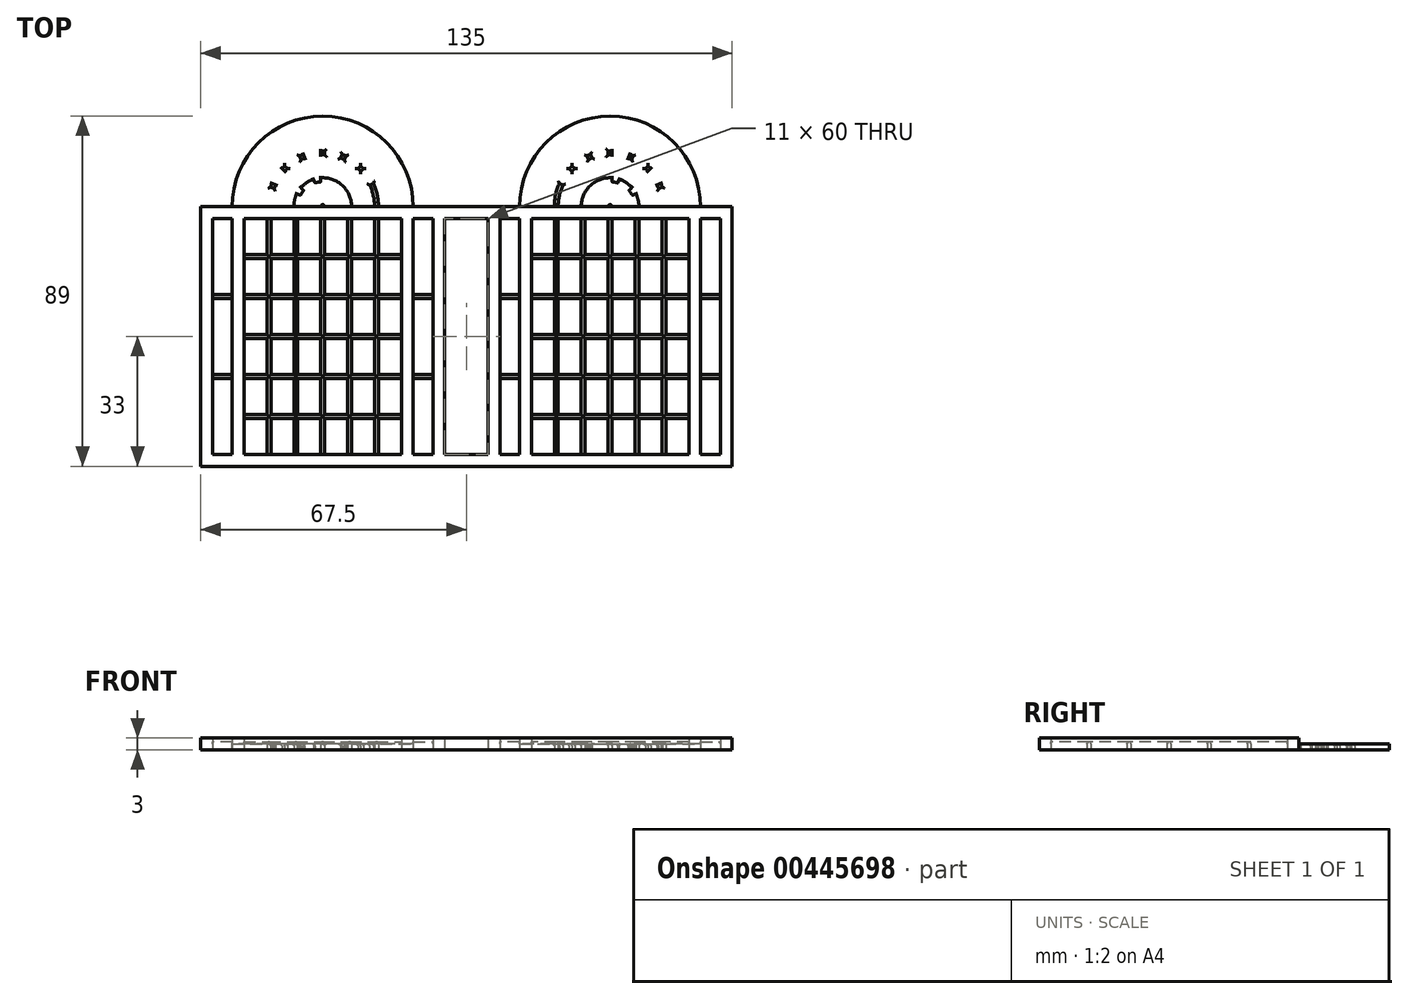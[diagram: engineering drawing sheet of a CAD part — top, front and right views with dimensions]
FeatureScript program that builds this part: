
annotation { "Feature Type Name" : "Feature", "Feature Type Description" : "" }
export const myFeature = defineFeature(function(context is Context, id is Id, definition is map)
    precondition{}
    {
        {
            var Q0;
            Q0=qCreatedBy(makeId("Top.planeOp"),FACE);
            var sketch = newSketch(context, id + "F0", { "sketchPlane" : qUnion([Q0])});
            skLineSegment(sketch, "E0.bottom", {"start": v(0, 0) * mm, "end": v(62, 0) * mm});
            skLineSegment(sketch, "E0.top", {"start": v(0, 60) * mm, "end": v(62, 60) * mm});
            skLineSegment(sketch, "E0.left", {"start": v(0, 0) * mm, "end": v(0, 60) * mm});
            skLineSegment(sketch, "E0.right", {"start": v(62, 0) * mm, "end": v(62, 60) * mm});
            skLineSegment(sketch, "E1", {"start": v(0, 0) * mm, "end": v(8, 0) * mm, "construction": true});
            skLineSegment(sketch, "E2", {"start": v(62, 0) * mm, "end": v(54, 0) * mm, "construction": true});
            skLineSegment(sketch, "E3", {"start": v(62, 0) * mm, "end": v(59, 0) * mm, "construction": true});
            skLineSegment(sketch, "E4", {"start": v(59, 0) * mm, "end": v(59, 60) * mm});
            skLineSegment(sketch, "E5", {"start": v(0, 60) * mm, "end": v(3, 60) * mm, "construction": true});
            skLineSegment(sketch, "E6", {"start": v(3, 60) * mm, "end": v(3, 0) * mm});
            skLineSegment(sketch, "E7", {"start": v(8, 0) * mm, "end": v(8, 60) * mm});
            skLineSegment(sketch, "E8", {"start": v(54, 0) * mm, "end": v(54, 60) * mm});
            skLineSegment(sketch, "E9", {"start": v(8, 0) * mm, "end": v(11, 0) * mm, "construction": true});
            skLineSegment(sketch, "E10", {"start": v(54, 0) * mm, "end": v(51, 0) * mm, "construction": true});
            skLineSegment(sketch, "E11", {"start": v(11, 0) * mm, "end": v(11, 60) * mm});
            skLineSegment(sketch, "E12", {"start": v(51, 0) * mm, "end": v(51, 60) * mm});
            skLineSegment(sketch, "E13.bottom", {"start": v(51, 0) * mm, "end": v(45.17, 0) * mm});
            skLineSegment(sketch, "E13.top", {"start": v(51, 9.17) * mm, "end": v(45.17, 9.17) * mm});
            skLineSegment(sketch, "E13.left", {"start": v(51, 0) * mm, "end": v(51, 9.17) * mm});
            skLineSegment(sketch, "E13.right", {"start": v(45.17, 0) * mm, "end": v(45.17, 9.17) * mm});
            skLineSegment(sketch, "E14.bottom", {"start": v(45.17, 0) * mm, "end": v(44.17, 0) * mm});
            skLineSegment(sketch, "E14.top", {"start": v(45.17, 9.17) * mm, "end": v(44.17, 9.17) * mm, "construction": true});
            skLineSegment(sketch, "E14.right", {"start": v(44.17, 0) * mm, "end": v(44.17, 9.17) * mm});
            skLineSegment(sketch, "E15.top", {"start": v(51, 10.17) * mm, "end": v(45.17, 10.17) * mm});
            skLineSegment(sketch, "E15.left", {"start": v(51, 9.17) * mm, "end": v(51, 10.17) * mm});
            skLineSegment(sketch, "E15.right", {"start": v(45.17, 9.17) * mm, "end": v(45.17, 10.17) * mm, "construction": true});
            skLineSegment(sketch, "E16", {"start": v(44.17, 9.17) * mm, "end": v(44.17, 10.17) * mm, "construction": true});
            skLineSegment(sketch, "E17", {"start": v(44.17, 10.17) * mm, "end": v(45.17, 10.17) * mm, "construction": true});
            skLineSegment(sketch, "E18.0.1.0", {"start": v(44.17, 20.33) * mm, "end": v(45.17, 20.33) * mm, "construction": true});
            skLineSegment(sketch, "E18.0.1.1", {"start": v(51, 20.33) * mm, "end": v(45.17, 20.33) * mm});
            skLineSegment(sketch, "E18.0.1.2", {"start": v(51, 19.33) * mm, "end": v(45.17, 19.33) * mm});
            skLineSegment(sketch, "E18.0.1.3", {"start": v(45.17, 10.17) * mm, "end": v(45.17, 19.33) * mm});
            skLineSegment(sketch, "E18.0.1.4", {"start": v(44.17, 10.17) * mm, "end": v(44.17, 19.33) * mm});
            skLineSegment(sketch, "E18.0.1.5", {"start": v(45.17, 19.33) * mm, "end": v(44.17, 19.33) * mm, "construction": true});
            skLineSegment(sketch, "E18.0.1.6", {"start": v(44.17, 19.33) * mm, "end": v(44.17, 20.33) * mm, "construction": true});
            skLineSegment(sketch, "E18.0.1.7", {"start": v(45.17, 19.33) * mm, "end": v(45.17, 20.33) * mm, "construction": true});
            skLineSegment(sketch, "E18.0.2.0", {"start": v(44.17, 30.5) * mm, "end": v(45.17, 30.5) * mm, "construction": true});
            skLineSegment(sketch, "E18.0.2.1", {"start": v(51, 30.5) * mm, "end": v(45.17, 30.5) * mm});
            skLineSegment(sketch, "E18.0.2.2", {"start": v(51, 29.5) * mm, "end": v(45.17, 29.5) * mm});
            skLineSegment(sketch, "E18.0.2.3", {"start": v(45.17, 20.33) * mm, "end": v(45.17, 29.5) * mm});
            skLineSegment(sketch, "E18.0.2.4", {"start": v(44.17, 20.33) * mm, "end": v(44.17, 29.5) * mm});
            skLineSegment(sketch, "E18.0.2.5", {"start": v(45.17, 29.5) * mm, "end": v(44.17, 29.5) * mm, "construction": true});
            skLineSegment(sketch, "E18.0.2.6", {"start": v(44.17, 29.5) * mm, "end": v(44.17, 30.5) * mm, "construction": true});
            skLineSegment(sketch, "E18.0.2.7", {"start": v(45.17, 29.5) * mm, "end": v(45.17, 30.5) * mm, "construction": true});
            skLineSegment(sketch, "E18.0.3.0", {"start": v(44.17, 40.67) * mm, "end": v(45.17, 40.67) * mm, "construction": true});
            skLineSegment(sketch, "E18.0.3.1", {"start": v(51, 40.67) * mm, "end": v(45.17, 40.67) * mm});
            skLineSegment(sketch, "E18.0.3.2", {"start": v(51, 39.67) * mm, "end": v(45.17, 39.67) * mm});
            skLineSegment(sketch, "E18.0.3.3", {"start": v(45.17, 30.5) * mm, "end": v(45.17, 39.67) * mm});
            skLineSegment(sketch, "E18.0.3.4", {"start": v(44.17, 30.5) * mm, "end": v(44.17, 39.67) * mm});
            skLineSegment(sketch, "E18.0.3.5", {"start": v(45.17, 39.67) * mm, "end": v(44.17, 39.67) * mm, "construction": true});
            skLineSegment(sketch, "E18.0.3.6", {"start": v(44.17, 39.67) * mm, "end": v(44.17, 40.67) * mm, "construction": true});
            skLineSegment(sketch, "E18.0.3.7", {"start": v(45.17, 39.67) * mm, "end": v(45.17, 40.67) * mm, "construction": true});
            skLineSegment(sketch, "E18.0.4.0", {"start": v(44.17, 50.83) * mm, "end": v(45.17, 50.83) * mm, "construction": true});
            skLineSegment(sketch, "E18.0.4.1", {"start": v(51, 50.83) * mm, "end": v(45.17, 50.83) * mm});
            skLineSegment(sketch, "E18.0.4.2", {"start": v(51, 49.83) * mm, "end": v(45.17, 49.83) * mm});
            skLineSegment(sketch, "E18.0.4.3", {"start": v(45.17, 40.67) * mm, "end": v(45.17, 49.83) * mm});
            skLineSegment(sketch, "E18.0.4.4", {"start": v(44.17, 40.67) * mm, "end": v(44.17, 49.83) * mm});
            skLineSegment(sketch, "E18.0.4.5", {"start": v(45.17, 49.83) * mm, "end": v(44.17, 49.83) * mm, "construction": true});
            skLineSegment(sketch, "E18.0.4.6", {"start": v(44.17, 49.83) * mm, "end": v(44.17, 50.83) * mm, "construction": true});
            skLineSegment(sketch, "E18.0.4.7", {"start": v(45.17, 49.83) * mm, "end": v(45.17, 50.83) * mm, "construction": true});
            skLineSegment(sketch, "E18.0.5.2", {"start": v(51, 60) * mm, "end": v(45.17, 60) * mm});
            skLineSegment(sketch, "E18.0.5.3", {"start": v(45.17, 50.83) * mm, "end": v(45.17, 60) * mm});
            skLineSegment(sketch, "E18.0.5.4", {"start": v(44.17, 50.83) * mm, "end": v(44.17, 60) * mm});
            skLineSegment(sketch, "E18.0.5.5", {"start": v(45.17, 60) * mm, "end": v(44.17, 60) * mm, "construction": true});
            skLineSegment(sketch, "E18.1.0.0", {"start": v(37.33, 10.17) * mm, "end": v(38.33, 10.17) * mm, "construction": true});
            skLineSegment(sketch, "E18.1.0.1", {"start": v(44.17, 10.17) * mm, "end": v(38.33, 10.17) * mm});
            skLineSegment(sketch, "E18.1.0.2", {"start": v(44.17, 9.17) * mm, "end": v(38.33, 9.17) * mm});
            skLineSegment(sketch, "E18.1.0.3", {"start": v(38.33, 0) * mm, "end": v(38.33, 9.17) * mm});
            skLineSegment(sketch, "E18.1.0.4", {"start": v(37.33, 0) * mm, "end": v(37.33, 9.17) * mm});
            skLineSegment(sketch, "E18.1.0.5", {"start": v(38.33, 9.17) * mm, "end": v(37.33, 9.17) * mm, "construction": true});
            skLineSegment(sketch, "E18.1.0.6", {"start": v(37.33, 9.17) * mm, "end": v(37.33, 10.17) * mm, "construction": true});
            skLineSegment(sketch, "E18.1.0.7", {"start": v(38.33, 9.17) * mm, "end": v(38.33, 10.17) * mm, "construction": true});
            skLineSegment(sketch, "E18.1.1.0", {"start": v(37.33, 20.33) * mm, "end": v(38.33, 20.33) * mm, "construction": true});
            skLineSegment(sketch, "E18.1.1.1", {"start": v(44.17, 20.33) * mm, "end": v(38.33, 20.33) * mm});
            skLineSegment(sketch, "E18.1.1.2", {"start": v(44.17, 19.33) * mm, "end": v(38.33, 19.33) * mm});
            skLineSegment(sketch, "E18.1.1.3", {"start": v(38.33, 10.17) * mm, "end": v(38.33, 19.33) * mm});
            skLineSegment(sketch, "E18.1.1.4", {"start": v(37.33, 10.17) * mm, "end": v(37.33, 19.33) * mm});
            skLineSegment(sketch, "E18.1.1.5", {"start": v(38.33, 19.33) * mm, "end": v(37.33, 19.33) * mm, "construction": true});
            skLineSegment(sketch, "E18.1.1.6", {"start": v(37.33, 19.33) * mm, "end": v(37.33, 20.33) * mm, "construction": true});
            skLineSegment(sketch, "E18.1.1.7", {"start": v(38.33, 19.33) * mm, "end": v(38.33, 20.33) * mm, "construction": true});
            skLineSegment(sketch, "E18.1.2.0", {"start": v(37.33, 30.5) * mm, "end": v(38.33, 30.5) * mm, "construction": true});
            skLineSegment(sketch, "E18.1.2.1", {"start": v(44.17, 30.5) * mm, "end": v(38.33, 30.5) * mm});
            skLineSegment(sketch, "E18.1.2.2", {"start": v(44.17, 29.5) * mm, "end": v(38.33, 29.5) * mm});
            skLineSegment(sketch, "E18.1.2.3", {"start": v(38.33, 20.33) * mm, "end": v(38.33, 29.5) * mm});
            skLineSegment(sketch, "E18.1.2.4", {"start": v(37.33, 20.33) * mm, "end": v(37.33, 29.5) * mm});
            skLineSegment(sketch, "E18.1.2.5", {"start": v(38.33, 29.5) * mm, "end": v(37.33, 29.5) * mm, "construction": true});
            skLineSegment(sketch, "E18.1.2.6", {"start": v(37.33, 29.5) * mm, "end": v(37.33, 30.5) * mm, "construction": true});
            skLineSegment(sketch, "E18.1.2.7", {"start": v(38.33, 29.5) * mm, "end": v(38.33, 30.5) * mm, "construction": true});
            skLineSegment(sketch, "E18.1.3.0", {"start": v(37.33, 40.67) * mm, "end": v(38.33, 40.67) * mm, "construction": true});
            skLineSegment(sketch, "E18.1.3.1", {"start": v(44.17, 40.67) * mm, "end": v(38.33, 40.67) * mm});
            skLineSegment(sketch, "E18.1.3.2", {"start": v(44.17, 39.67) * mm, "end": v(38.33, 39.67) * mm});
            skLineSegment(sketch, "E18.1.3.3", {"start": v(38.33, 30.5) * mm, "end": v(38.33, 39.67) * mm});
            skLineSegment(sketch, "E18.1.3.4", {"start": v(37.33, 30.5) * mm, "end": v(37.33, 39.67) * mm});
            skLineSegment(sketch, "E18.1.3.5", {"start": v(38.33, 39.67) * mm, "end": v(37.33, 39.67) * mm, "construction": true});
            skLineSegment(sketch, "E18.1.3.6", {"start": v(37.33, 39.67) * mm, "end": v(37.33, 40.67) * mm, "construction": true});
            skLineSegment(sketch, "E18.1.3.7", {"start": v(38.33, 39.67) * mm, "end": v(38.33, 40.67) * mm, "construction": true});
            skLineSegment(sketch, "E18.1.4.0", {"start": v(37.33, 50.83) * mm, "end": v(38.33, 50.83) * mm, "construction": true});
            skLineSegment(sketch, "E18.1.4.1", {"start": v(44.17, 50.83) * mm, "end": v(38.33, 50.83) * mm});
            skLineSegment(sketch, "E18.1.4.2", {"start": v(44.17, 49.83) * mm, "end": v(38.33, 49.83) * mm});
            skLineSegment(sketch, "E18.1.4.3", {"start": v(38.33, 40.67) * mm, "end": v(38.33, 49.83) * mm});
            skLineSegment(sketch, "E18.1.4.4", {"start": v(37.33, 40.67) * mm, "end": v(37.33, 49.83) * mm});
            skLineSegment(sketch, "E18.1.4.5", {"start": v(38.33, 49.83) * mm, "end": v(37.33, 49.83) * mm, "construction": true});
            skLineSegment(sketch, "E18.1.4.6", {"start": v(37.33, 49.83) * mm, "end": v(37.33, 50.83) * mm, "construction": true});
            skLineSegment(sketch, "E18.1.4.7", {"start": v(38.33, 49.83) * mm, "end": v(38.33, 50.83) * mm, "construction": true});
            skLineSegment(sketch, "E18.1.5.2", {"start": v(44.17, 60) * mm, "end": v(38.33, 60) * mm});
            skLineSegment(sketch, "E18.1.5.3", {"start": v(38.33, 50.83) * mm, "end": v(38.33, 60) * mm});
            skLineSegment(sketch, "E18.1.5.4", {"start": v(37.33, 50.83) * mm, "end": v(37.33, 60) * mm});
            skLineSegment(sketch, "E18.1.5.5", {"start": v(38.33, 60) * mm, "end": v(37.33, 60) * mm, "construction": true});
            skLineSegment(sketch, "E18.2.0.0", {"start": v(30.5, 10.17) * mm, "end": v(31.5, 10.17) * mm, "construction": true});
            skLineSegment(sketch, "E18.2.0.1", {"start": v(37.33, 10.17) * mm, "end": v(31.5, 10.17) * mm});
            skLineSegment(sketch, "E18.2.0.2", {"start": v(37.33, 9.17) * mm, "end": v(31.5, 9.17) * mm});
            skLineSegment(sketch, "E18.2.0.3", {"start": v(31.5, 0) * mm, "end": v(31.5, 9.17) * mm});
            skLineSegment(sketch, "E18.2.0.4", {"start": v(30.5, 0) * mm, "end": v(30.5, 9.17) * mm});
            skLineSegment(sketch, "E18.2.0.5", {"start": v(31.5, 9.17) * mm, "end": v(30.5, 9.17) * mm, "construction": true});
            skLineSegment(sketch, "E18.2.0.6", {"start": v(30.5, 9.17) * mm, "end": v(30.5, 10.17) * mm, "construction": true});
            skLineSegment(sketch, "E18.2.0.7", {"start": v(31.5, 9.17) * mm, "end": v(31.5, 10.17) * mm, "construction": true});
            skLineSegment(sketch, "E18.2.1.0", {"start": v(30.5, 20.33) * mm, "end": v(31.5, 20.33) * mm, "construction": true});
            skLineSegment(sketch, "E18.2.1.1", {"start": v(37.33, 20.33) * mm, "end": v(31.5, 20.33) * mm});
            skLineSegment(sketch, "E18.2.1.2", {"start": v(37.33, 19.33) * mm, "end": v(31.5, 19.33) * mm});
            skLineSegment(sketch, "E18.2.1.3", {"start": v(31.5, 10.17) * mm, "end": v(31.5, 19.33) * mm});
            skLineSegment(sketch, "E18.2.1.4", {"start": v(30.5, 10.17) * mm, "end": v(30.5, 19.33) * mm});
            skLineSegment(sketch, "E18.2.1.5", {"start": v(31.5, 19.33) * mm, "end": v(30.5, 19.33) * mm, "construction": true});
            skLineSegment(sketch, "E18.2.1.6", {"start": v(30.5, 19.33) * mm, "end": v(30.5, 20.33) * mm, "construction": true});
            skLineSegment(sketch, "E18.2.1.7", {"start": v(31.5, 19.33) * mm, "end": v(31.5, 20.33) * mm, "construction": true});
            skLineSegment(sketch, "E18.2.2.0", {"start": v(30.5, 30.5) * mm, "end": v(31.5, 30.5) * mm, "construction": true});
            skLineSegment(sketch, "E18.2.2.1", {"start": v(37.33, 30.5) * mm, "end": v(31.5, 30.5) * mm});
            skLineSegment(sketch, "E18.2.2.2", {"start": v(37.33, 29.5) * mm, "end": v(31.5, 29.5) * mm});
            skLineSegment(sketch, "E18.2.2.3", {"start": v(31.5, 20.33) * mm, "end": v(31.5, 29.5) * mm});
            skLineSegment(sketch, "E18.2.2.4", {"start": v(30.5, 20.33) * mm, "end": v(30.5, 29.5) * mm});
            skLineSegment(sketch, "E18.2.2.5", {"start": v(31.5, 29.5) * mm, "end": v(30.5, 29.5) * mm, "construction": true});
            skLineSegment(sketch, "E18.2.2.6", {"start": v(30.5, 29.5) * mm, "end": v(30.5, 30.5) * mm, "construction": true});
            skLineSegment(sketch, "E18.2.2.7", {"start": v(31.5, 29.5) * mm, "end": v(31.5, 30.5) * mm, "construction": true});
            skLineSegment(sketch, "E18.2.3.0", {"start": v(30.5, 40.67) * mm, "end": v(31.5, 40.67) * mm, "construction": true});
            skLineSegment(sketch, "E18.2.3.1", {"start": v(37.33, 40.67) * mm, "end": v(31.5, 40.67) * mm});
            skLineSegment(sketch, "E18.2.3.2", {"start": v(37.33, 39.67) * mm, "end": v(31.5, 39.67) * mm});
            skLineSegment(sketch, "E18.2.3.3", {"start": v(31.5, 30.5) * mm, "end": v(31.5, 39.67) * mm});
            skLineSegment(sketch, "E18.2.3.4", {"start": v(30.5, 30.5) * mm, "end": v(30.5, 39.67) * mm});
            skLineSegment(sketch, "E18.2.3.5", {"start": v(31.5, 39.67) * mm, "end": v(30.5, 39.67) * mm, "construction": true});
            skLineSegment(sketch, "E18.2.3.6", {"start": v(30.5, 39.67) * mm, "end": v(30.5, 40.67) * mm, "construction": true});
            skLineSegment(sketch, "E18.2.3.7", {"start": v(31.5, 39.67) * mm, "end": v(31.5, 40.67) * mm, "construction": true});
            skLineSegment(sketch, "E18.2.4.0", {"start": v(30.5, 50.83) * mm, "end": v(31.5, 50.83) * mm, "construction": true});
            skLineSegment(sketch, "E18.2.4.1", {"start": v(37.33, 50.83) * mm, "end": v(31.5, 50.83) * mm});
            skLineSegment(sketch, "E18.2.4.2", {"start": v(37.33, 49.83) * mm, "end": v(31.5, 49.83) * mm});
            skLineSegment(sketch, "E18.2.4.3", {"start": v(31.5, 40.67) * mm, "end": v(31.5, 49.83) * mm});
            skLineSegment(sketch, "E18.2.4.4", {"start": v(30.5, 40.67) * mm, "end": v(30.5, 49.83) * mm});
            skLineSegment(sketch, "E18.2.4.5", {"start": v(31.5, 49.83) * mm, "end": v(30.5, 49.83) * mm, "construction": true});
            skLineSegment(sketch, "E18.2.4.6", {"start": v(30.5, 49.83) * mm, "end": v(30.5, 50.83) * mm, "construction": true});
            skLineSegment(sketch, "E18.2.4.7", {"start": v(31.5, 49.83) * mm, "end": v(31.5, 50.83) * mm, "construction": true});
            skLineSegment(sketch, "E18.2.5.2", {"start": v(37.33, 60) * mm, "end": v(31.5, 60) * mm});
            skLineSegment(sketch, "E18.2.5.3", {"start": v(31.5, 50.83) * mm, "end": v(31.5, 60) * mm});
            skLineSegment(sketch, "E18.2.5.4", {"start": v(30.5, 50.83) * mm, "end": v(30.5, 60) * mm});
            skLineSegment(sketch, "E18.2.5.5", {"start": v(31.5, 60) * mm, "end": v(30.5, 60) * mm, "construction": true});
            skLineSegment(sketch, "E18.3.0.0", {"start": v(23.67, 10.17) * mm, "end": v(24.67, 10.17) * mm, "construction": true});
            skLineSegment(sketch, "E18.3.0.1", {"start": v(30.5, 10.17) * mm, "end": v(24.67, 10.17) * mm});
            skLineSegment(sketch, "E18.3.0.2", {"start": v(30.5, 9.17) * mm, "end": v(24.67, 9.17) * mm});
            skLineSegment(sketch, "E18.3.0.3", {"start": v(24.67, 0) * mm, "end": v(24.67, 9.17) * mm});
            skLineSegment(sketch, "E18.3.0.4", {"start": v(23.67, 0) * mm, "end": v(23.67, 9.17) * mm});
            skLineSegment(sketch, "E18.3.0.5", {"start": v(24.67, 9.17) * mm, "end": v(23.67, 9.17) * mm, "construction": true});
            skLineSegment(sketch, "E18.3.0.6", {"start": v(23.67, 9.17) * mm, "end": v(23.67, 10.17) * mm, "construction": true});
            skLineSegment(sketch, "E18.3.0.7", {"start": v(24.67, 9.17) * mm, "end": v(24.67, 10.17) * mm, "construction": true});
            skLineSegment(sketch, "E18.3.1.0", {"start": v(23.67, 20.33) * mm, "end": v(24.67, 20.33) * mm, "construction": true});
            skLineSegment(sketch, "E18.3.1.1", {"start": v(30.5, 20.33) * mm, "end": v(24.67, 20.33) * mm});
            skLineSegment(sketch, "E18.3.1.2", {"start": v(30.5, 19.33) * mm, "end": v(24.67, 19.33) * mm});
            skLineSegment(sketch, "E18.3.1.3", {"start": v(24.67, 10.17) * mm, "end": v(24.67, 19.33) * mm});
            skLineSegment(sketch, "E18.3.1.4", {"start": v(23.67, 10.17) * mm, "end": v(23.67, 19.33) * mm});
            skLineSegment(sketch, "E18.3.1.5", {"start": v(24.67, 19.33) * mm, "end": v(23.67, 19.33) * mm, "construction": true});
            skLineSegment(sketch, "E18.3.1.6", {"start": v(23.67, 19.33) * mm, "end": v(23.67, 20.33) * mm, "construction": true});
            skLineSegment(sketch, "E18.3.1.7", {"start": v(24.67, 19.33) * mm, "end": v(24.67, 20.33) * mm, "construction": true});
            skLineSegment(sketch, "E18.3.2.0", {"start": v(23.67, 30.5) * mm, "end": v(24.67, 30.5) * mm, "construction": true});
            skLineSegment(sketch, "E18.3.2.1", {"start": v(30.5, 30.5) * mm, "end": v(24.67, 30.5) * mm});
            skLineSegment(sketch, "E18.3.2.2", {"start": v(30.5, 29.5) * mm, "end": v(24.67, 29.5) * mm});
            skLineSegment(sketch, "E18.3.2.3", {"start": v(24.67, 20.33) * mm, "end": v(24.67, 29.5) * mm});
            skLineSegment(sketch, "E18.3.2.4", {"start": v(23.67, 20.33) * mm, "end": v(23.67, 29.5) * mm});
            skLineSegment(sketch, "E18.3.2.5", {"start": v(24.67, 29.5) * mm, "end": v(23.67, 29.5) * mm, "construction": true});
            skLineSegment(sketch, "E18.3.2.6", {"start": v(23.67, 29.5) * mm, "end": v(23.67, 30.5) * mm, "construction": true});
            skLineSegment(sketch, "E18.3.2.7", {"start": v(24.67, 29.5) * mm, "end": v(24.67, 30.5) * mm, "construction": true});
            skLineSegment(sketch, "E18.3.3.0", {"start": v(23.67, 40.67) * mm, "end": v(24.67, 40.67) * mm, "construction": true});
            skLineSegment(sketch, "E18.3.3.1", {"start": v(30.5, 40.67) * mm, "end": v(24.67, 40.67) * mm});
            skLineSegment(sketch, "E18.3.3.2", {"start": v(30.5, 39.67) * mm, "end": v(24.67, 39.67) * mm});
            skLineSegment(sketch, "E18.3.3.3", {"start": v(24.67, 30.5) * mm, "end": v(24.67, 39.67) * mm});
            skLineSegment(sketch, "E18.3.3.4", {"start": v(23.67, 30.5) * mm, "end": v(23.67, 39.67) * mm});
            skLineSegment(sketch, "E18.3.3.5", {"start": v(24.67, 39.67) * mm, "end": v(23.67, 39.67) * mm, "construction": true});
            skLineSegment(sketch, "E18.3.3.6", {"start": v(23.67, 39.67) * mm, "end": v(23.67, 40.67) * mm, "construction": true});
            skLineSegment(sketch, "E18.3.3.7", {"start": v(24.67, 39.67) * mm, "end": v(24.67, 40.67) * mm, "construction": true});
            skLineSegment(sketch, "E18.3.4.0", {"start": v(23.67, 50.83) * mm, "end": v(24.67, 50.83) * mm, "construction": true});
            skLineSegment(sketch, "E18.3.4.1", {"start": v(30.5, 50.83) * mm, "end": v(24.67, 50.83) * mm});
            skLineSegment(sketch, "E18.3.4.2", {"start": v(30.5, 49.83) * mm, "end": v(24.67, 49.83) * mm});
            skLineSegment(sketch, "E18.3.4.3", {"start": v(24.67, 40.67) * mm, "end": v(24.67, 49.83) * mm});
            skLineSegment(sketch, "E18.3.4.4", {"start": v(23.67, 40.67) * mm, "end": v(23.67, 49.83) * mm});
            skLineSegment(sketch, "E18.3.4.5", {"start": v(24.67, 49.83) * mm, "end": v(23.67, 49.83) * mm, "construction": true});
            skLineSegment(sketch, "E18.3.4.6", {"start": v(23.67, 49.83) * mm, "end": v(23.67, 50.83) * mm, "construction": true});
            skLineSegment(sketch, "E18.3.4.7", {"start": v(24.67, 49.83) * mm, "end": v(24.67, 50.83) * mm, "construction": true});
            skLineSegment(sketch, "E18.3.5.2", {"start": v(30.5, 60) * mm, "end": v(24.67, 60) * mm});
            skLineSegment(sketch, "E18.3.5.3", {"start": v(24.67, 50.83) * mm, "end": v(24.67, 60) * mm});
            skLineSegment(sketch, "E18.3.5.4", {"start": v(23.67, 50.83) * mm, "end": v(23.67, 60) * mm});
            skLineSegment(sketch, "E18.3.5.5", {"start": v(24.67, 60) * mm, "end": v(23.67, 60) * mm, "construction": true});
            skLineSegment(sketch, "E18.4.0.0", {"start": v(16.83, 10.17) * mm, "end": v(17.83, 10.17) * mm, "construction": true});
            skLineSegment(sketch, "E18.4.0.1", {"start": v(23.67, 10.17) * mm, "end": v(17.83, 10.17) * mm});
            skLineSegment(sketch, "E18.4.0.2", {"start": v(23.67, 9.17) * mm, "end": v(17.83, 9.17) * mm});
            skLineSegment(sketch, "E18.4.0.3", {"start": v(17.83, 0) * mm, "end": v(17.83, 9.17) * mm});
            skLineSegment(sketch, "E18.4.0.4", {"start": v(16.83, 0) * mm, "end": v(16.83, 9.17) * mm});
            skLineSegment(sketch, "E18.4.0.5", {"start": v(17.83, 9.17) * mm, "end": v(16.83, 9.17) * mm, "construction": true});
            skLineSegment(sketch, "E18.4.0.6", {"start": v(16.83, 9.17) * mm, "end": v(16.83, 10.17) * mm, "construction": true});
            skLineSegment(sketch, "E18.4.0.7", {"start": v(17.83, 9.17) * mm, "end": v(17.83, 10.17) * mm, "construction": true});
            skLineSegment(sketch, "E18.4.1.0", {"start": v(16.83, 20.33) * mm, "end": v(17.83, 20.33) * mm, "construction": true});
            skLineSegment(sketch, "E18.4.1.1", {"start": v(23.67, 20.33) * mm, "end": v(17.83, 20.33) * mm});
            skLineSegment(sketch, "E18.4.1.2", {"start": v(23.67, 19.33) * mm, "end": v(17.83, 19.33) * mm});
            skLineSegment(sketch, "E18.4.1.3", {"start": v(17.83, 10.17) * mm, "end": v(17.83, 19.33) * mm});
            skLineSegment(sketch, "E18.4.1.4", {"start": v(16.83, 10.17) * mm, "end": v(16.83, 19.33) * mm});
            skLineSegment(sketch, "E18.4.1.5", {"start": v(17.83, 19.33) * mm, "end": v(16.83, 19.33) * mm, "construction": true});
            skLineSegment(sketch, "E18.4.1.6", {"start": v(16.83, 19.33) * mm, "end": v(16.83, 20.33) * mm, "construction": true});
            skLineSegment(sketch, "E18.4.1.7", {"start": v(17.83, 19.33) * mm, "end": v(17.83, 20.33) * mm, "construction": true});
            skLineSegment(sketch, "E18.4.2.0", {"start": v(16.83, 30.5) * mm, "end": v(17.83, 30.5) * mm, "construction": true});
            skLineSegment(sketch, "E18.4.2.1", {"start": v(23.67, 30.5) * mm, "end": v(17.83, 30.5) * mm});
            skLineSegment(sketch, "E18.4.2.2", {"start": v(23.67, 29.5) * mm, "end": v(17.83, 29.5) * mm});
            skLineSegment(sketch, "E18.4.2.3", {"start": v(17.83, 20.33) * mm, "end": v(17.83, 29.5) * mm});
            skLineSegment(sketch, "E18.4.2.4", {"start": v(16.83, 20.33) * mm, "end": v(16.83, 29.5) * mm});
            skLineSegment(sketch, "E18.4.2.5", {"start": v(17.83, 29.5) * mm, "end": v(16.83, 29.5) * mm, "construction": true});
            skLineSegment(sketch, "E18.4.2.6", {"start": v(16.83, 29.5) * mm, "end": v(16.83, 30.5) * mm, "construction": true});
            skLineSegment(sketch, "E18.4.2.7", {"start": v(17.83, 29.5) * mm, "end": v(17.83, 30.5) * mm, "construction": true});
            skLineSegment(sketch, "E18.4.3.0", {"start": v(16.83, 40.67) * mm, "end": v(17.83, 40.67) * mm, "construction": true});
            skLineSegment(sketch, "E18.4.3.1", {"start": v(23.67, 40.67) * mm, "end": v(17.83, 40.67) * mm});
            skLineSegment(sketch, "E18.4.3.2", {"start": v(23.67, 39.67) * mm, "end": v(17.83, 39.67) * mm});
            skLineSegment(sketch, "E18.4.3.3", {"start": v(17.83, 30.5) * mm, "end": v(17.83, 39.67) * mm});
            skLineSegment(sketch, "E18.4.3.4", {"start": v(16.83, 30.5) * mm, "end": v(16.83, 39.67) * mm});
            skLineSegment(sketch, "E18.4.3.5", {"start": v(17.83, 39.67) * mm, "end": v(16.83, 39.67) * mm, "construction": true});
            skLineSegment(sketch, "E18.4.3.6", {"start": v(16.83, 39.67) * mm, "end": v(16.83, 40.67) * mm, "construction": true});
            skLineSegment(sketch, "E18.4.3.7", {"start": v(17.83, 39.67) * mm, "end": v(17.83, 40.67) * mm, "construction": true});
            skLineSegment(sketch, "E18.4.4.0", {"start": v(16.83, 50.83) * mm, "end": v(17.83, 50.83) * mm, "construction": true});
            skLineSegment(sketch, "E18.4.4.1", {"start": v(23.67, 50.83) * mm, "end": v(17.83, 50.83) * mm});
            skLineSegment(sketch, "E18.4.4.2", {"start": v(23.67, 49.83) * mm, "end": v(17.83, 49.83) * mm});
            skLineSegment(sketch, "E18.4.4.3", {"start": v(17.83, 40.67) * mm, "end": v(17.83, 49.83) * mm});
            skLineSegment(sketch, "E18.4.4.4", {"start": v(16.83, 40.67) * mm, "end": v(16.83, 49.83) * mm});
            skLineSegment(sketch, "E18.4.4.5", {"start": v(17.83, 49.83) * mm, "end": v(16.83, 49.83) * mm, "construction": true});
            skLineSegment(sketch, "E18.4.4.6", {"start": v(16.83, 49.83) * mm, "end": v(16.83, 50.83) * mm, "construction": true});
            skLineSegment(sketch, "E18.4.4.7", {"start": v(17.83, 49.83) * mm, "end": v(17.83, 50.83) * mm, "construction": true});
            skLineSegment(sketch, "E18.4.5.2", {"start": v(23.67, 60) * mm, "end": v(17.83, 60) * mm});
            skLineSegment(sketch, "E18.4.5.3", {"start": v(17.83, 50.83) * mm, "end": v(17.83, 60) * mm});
            skLineSegment(sketch, "E18.4.5.4", {"start": v(16.83, 50.83) * mm, "end": v(16.83, 60) * mm});
            skLineSegment(sketch, "E18.4.5.5", {"start": v(17.83, 60) * mm, "end": v(16.83, 60) * mm, "construction": true});
            skLineSegment(sketch, "E18.5.0.1", {"start": v(16.83, 10.17) * mm, "end": v(11, 10.17) * mm});
            skLineSegment(sketch, "E18.5.0.2", {"start": v(16.83, 9.17) * mm, "end": v(11, 9.17) * mm});
            skLineSegment(sketch, "E18.5.0.3", {"start": v(11, 0) * mm, "end": v(11, 9.17) * mm});
            skLineSegment(sketch, "E18.5.0.7", {"start": v(11, 9.17) * mm, "end": v(11, 10.17) * mm, "construction": true});
            skLineSegment(sketch, "E18.5.1.1", {"start": v(16.83, 20.33) * mm, "end": v(11, 20.33) * mm});
            skLineSegment(sketch, "E18.5.1.2", {"start": v(16.83, 19.33) * mm, "end": v(11, 19.33) * mm});
            skLineSegment(sketch, "E18.5.1.3", {"start": v(11, 10.17) * mm, "end": v(11, 19.33) * mm});
            skLineSegment(sketch, "E18.5.1.7", {"start": v(11, 19.33) * mm, "end": v(11, 20.33) * mm, "construction": true});
            skLineSegment(sketch, "E18.5.2.1", {"start": v(16.83, 30.5) * mm, "end": v(11, 30.5) * mm});
            skLineSegment(sketch, "E18.5.2.2", {"start": v(16.83, 29.5) * mm, "end": v(11, 29.5) * mm});
            skLineSegment(sketch, "E18.5.2.3", {"start": v(11, 20.33) * mm, "end": v(11, 29.5) * mm});
            skLineSegment(sketch, "E18.5.2.7", {"start": v(11, 29.5) * mm, "end": v(11, 30.5) * mm, "construction": true});
            skLineSegment(sketch, "E18.5.3.1", {"start": v(16.83, 40.67) * mm, "end": v(11, 40.67) * mm});
            skLineSegment(sketch, "E18.5.3.2", {"start": v(16.83, 39.67) * mm, "end": v(11, 39.67) * mm});
            skLineSegment(sketch, "E18.5.3.3", {"start": v(11, 30.5) * mm, "end": v(11, 39.67) * mm});
            skLineSegment(sketch, "E18.5.3.7", {"start": v(11, 39.67) * mm, "end": v(11, 40.67) * mm, "construction": true});
            skLineSegment(sketch, "E18.5.4.1", {"start": v(16.83, 50.83) * mm, "end": v(11, 50.83) * mm});
            skLineSegment(sketch, "E18.5.4.2", {"start": v(16.83, 49.83) * mm, "end": v(11, 49.83) * mm});
            skLineSegment(sketch, "E18.5.4.3", {"start": v(11, 40.67) * mm, "end": v(11, 49.83) * mm});
            skLineSegment(sketch, "E18.5.4.7", {"start": v(11, 49.83) * mm, "end": v(11, 50.83) * mm, "construction": true});
            skLineSegment(sketch, "E18.5.5.2", {"start": v(16.83, 60) * mm, "end": v(11, 60) * mm});
            skLineSegment(sketch, "E18.5.5.3", {"start": v(11, 50.83) * mm, "end": v(11, 60) * mm});
            skLineSegment(sketch, "E18.direction1", {"start": v(44.17, 0) * mm, "end": v(37.33, 0) * mm, "construction": true});
            skLineSegment(sketch, "E18.direction2", {"start": v(44.17, 0) * mm, "end": v(44.17, 10.17) * mm, "construction": true});
            skLineSegment(sketch, "E19.top", {"start": v(0, -3) * mm, "end": v(62, -3) * mm});
            skLineSegment(sketch, "E19.left", {"start": v(0, 0) * mm, "end": v(0, -3) * mm});
            skLineSegment(sketch, "E19.right", {"start": v(62, 0) * mm, "end": v(62, -3) * mm});
            skLineSegment(sketch, "E20.top", {"start": v(0, 63) * mm, "end": v(62, 63) * mm});
            skLineSegment(sketch, "E20.left", {"start": v(0, 60) * mm, "end": v(0, 63) * mm});
            skLineSegment(sketch, "E20.right", {"start": v(62, 60) * mm, "end": v(62, 63) * mm});
            skLineSegment(sketch, "E21", {"start": v(31, 63) * mm, "end": v(31, 86) * mm, "construction": true});
            skArc(sketch, "E22", {"start": v(11, 63) * mm, "mid": v(31, 83) * mm, "end": v(51, 63) * mm});
            skArc(sketch, "E23", {"start": v(8, 63) * mm, "mid": v(31, 86) * mm, "end": v(54, 63) * mm});
            skArc(sketch, "E24", {"start": v(16.83, 63) * mm, "mid": v(31, 77.17) * mm, "end": v(45.17, 63) * mm});
            skArc(sketch, "E25", {"start": v(17.83, 63) * mm, "mid": v(31, 76.17) * mm, "end": v(44.17, 63) * mm});
            skArc(sketch, "E26", {"start": v(23.67, 63) * mm, "mid": v(31, 70.33) * mm, "end": v(38.33, 63) * mm});
            skArc(sketch, "E27", {"start": v(24.67, 63) * mm, "mid": v(31, 69.33) * mm, "end": v(37.33, 63) * mm});
            skArc(sketch, "E28", {"start": v(30.5, 63) * mm, "mid": v(31, 63.5) * mm, "end": v(31.5, 63) * mm});
            skLineSegment(sketch, "E29", {"start": v(31, 63) * mm, "end": v(8, 63) * mm});
            skLineSegment(sketch, "E30.1.0", {"start": v(31, 63) * mm, "end": v(9.75, 71.8) * mm, "construction": true});
            skLineSegment(sketch, "E30.2.0", {"start": v(31, 63) * mm, "end": v(14.74, 79.26) * mm, "construction": true});
            skLineSegment(sketch, "E30.3.0", {"start": v(31, 63) * mm, "end": v(22.2, 84.25) * mm, "construction": true});
            skLineSegment(sketch, "E30.5.0", {"start": v(31, 63) * mm, "end": v(39.8, 84.25) * mm, "construction": true});
            skLineSegment(sketch, "E30.6.0", {"start": v(31, 63) * mm, "end": v(47.26, 79.26) * mm, "construction": true});
            skLineSegment(sketch, "E30.7.0", {"start": v(31, 63) * mm, "end": v(52.25, 71.8) * mm, "construction": true});
            skLineSegment(sketch, "E30.8.0", {"start": v(31, 63) * mm, "end": v(54, 63) * mm});
            skLineSegment(sketch, "E30.anchor1", {"start": v(31, 63) * mm, "end": v(8, 63) * mm, "construction": true});
            skLineSegment(sketch, "E30.anchor2", {"start": v(31, 63) * mm, "end": v(54, 63) * mm, "construction": true});
            skLineSegment(sketch, "E31.0", {"start": v(30.08, 63.92) * mm, "end": v(12.72, 71.11) * mm});
            skLineSegment(sketch, "E32.MirrorCS", {"start": v(29.7, 63) * mm, "end": v(12.34, 70.19) * mm});
            skLineSegment(sketch, "E33.0", {"start": v(30.5, 64.2) * mm, "end": v(17.22, 77.5) * mm});
            skLineSegment(sketch, "E34.MirrorCS", {"start": v(28.87, 64.42) * mm, "end": v(16.5, 76.78) * mm});
            skLineSegment(sketch, "E35.0", {"start": v(31, 64.3) * mm, "end": v(23.81, 81.66) * mm});
            skLineSegment(sketch, "E36.MirrorCS", {"start": v(30.08, 63.92) * mm, "end": v(22.89, 81.28) * mm});
            skLineSegment(sketch, "E37.0", {"start": v(31.5, 65.51) * mm, "end": v(31.5, 83) * mm});
            skLineSegment(sketch, "E38.0", {"start": v(30.5, 65.51) * mm, "end": v(30.5, 83) * mm});
            skLineSegment(sketch, "E39.0", {"start": v(32.42, 65.13) * mm, "end": v(39.11, 81.28) * mm});
            skLineSegment(sketch, "E40.0", {"start": v(31, 64.3) * mm, "end": v(38.19, 81.66) * mm});
            skLineSegment(sketch, "E41.0", {"start": v(32.3, 63) * mm, "end": v(49.66, 70.19) * mm});
            skLineSegment(sketch, "E42.0", {"start": v(33.13, 64.42) * mm, "end": v(49.28, 71.11) * mm});
            skLineSegment(sketch, "E43.0", {"start": v(33.13, 64.42) * mm, "end": v(45.5, 76.78) * mm});
            skLineSegment(sketch, "E44.0", {"start": v(32.42, 65.13) * mm, "end": v(44.78, 77.5) * mm});
            skSolve(sketch);
        }
        {
            var Q0;
            {var subQ13=sQuery(id+"F0.wireOp",EDGE,"E23");Q0=makeQuery(id+"F0.imprint","IMPRINT",FACE,{"disambiguationData":[TD([[makeQuery(id+"F0.imprint","IMPRINT",EDGE,{"derivedFrom":subQ13}),-1.0]])]});}
            var Q1;
            {var subQ1=sQuery(id+"F0.wireOp",EDGE,"E20.left");Q1=makeQuery(id+"F0.imprint","IMPRINT",FACE,{"disambiguationData":[TD([[makeQuery(id+"F0.imprint","IMPRINT",EDGE,{"derivedFrom":subQ1}),-1.0]])]});}
            var Q2;
            {var subQ0=sQuery(id+"F0.wireOp",EDGE,"E0.right");Q2=makeQuery(id+"F0.imprint","IMPRINT",FACE,{"disambiguationData":[TD([[makeQuery(id+"F0.imprint","IMPRINT",EDGE,{"derivedFrom":subQ0}),1.0]])]});}
            var Q3;
            {var subQ7=sQuery(id+"F0.wireOp",EDGE,"E7");Q3=makeQuery(id+"F0.imprint","IMPRINT",FACE,{"disambiguationData":[TD([[makeQuery(id+"F0.imprint","IMPRINT",EDGE,{"derivedFrom":subQ7}),-1.0]])]});}
            var Q4;
            {var subQ0=sQuery(id+"F0.wireOp",EDGE,"E0.left");Q4=makeQuery(id+"F0.imprint","IMPRINT",FACE,{"disambiguationData":[TD([[makeQuery(id+"F0.imprint","IMPRINT",EDGE,{"derivedFrom":subQ0}),-1.0]])]});}
            var Q5;
            {var subQ9=sQuery(id+"F0.wireOp",EDGE,"E8");Q5=makeQuery(id+"F0.imprint","IMPRINT",FACE,{"disambiguationData":[TD([[makeQuery(id+"F0.imprint","IMPRINT",EDGE,{"derivedFrom":subQ9}),1.0]])]});}
            var Q6;
            Q6=makeQuery(id+"F0.imprint","IMPRINT",FACE,{"disambiguationData":[TD([[makeQuery(id+"F0.imprint","IMPRINT",EDGE,{"derivedFrom":sQuery(id+"F0.wireOp",EDGE,"E19.top")}),1.0]])]});
            extrude(context, id + "F1", {"entities" : qUnion([Q0, Q1, Q2, Q3, Q4, Q5, Q6]), "depth" : 3 * mm});
        }
        {
            var Q0;
            {var subQ0=sQuery(id+"F0.wireOp",EDGE,"E29");var subQ1=sQuery(id+"F0.wireOp",EDGE,"E24");var subQ2=makeQuery(id+"F0.imprint","INTERSECT",VERTEX,{"derivedFrom":[subQ1,subQ0]});Q0=makeQuery(id+"F0.imprint","IMPRINT",FACE,{"disambiguationData":[TD([[makeQuery(id+"F0.imprint","IMPRINT",EDGE,{"disambiguationData":[TD([[subQ2,-1.0]])],"derivedFrom":subQ1}),-1.0]])]});}
            var Q1;
            {var subQ0=sQuery(id+"F0.wireOp",EDGE,"E31.0");var subQ1=sQuery(id+"F0.wireOp",EDGE,"E24");var subQ2=makeQuery(id+"F0.imprint","INTERSECT",VERTEX,{"derivedFrom":[subQ1,subQ0]});Q1=makeQuery(id+"F0.imprint","IMPRINT",FACE,{"disambiguationData":[TD([[makeQuery(id+"F0.imprint","IMPRINT",EDGE,{"disambiguationData":[TD([[subQ2,-1.0]])],"derivedFrom":subQ1}),-1.0]])]});}
            var Q2;
            {var subQ0=sQuery(id+"F0.wireOp",EDGE,"E35.0");var subQ1=sQuery(id+"F0.wireOp",EDGE,"E24");var subQ2=makeQuery(id+"F0.imprint","INTERSECT",VERTEX,{"derivedFrom":[subQ1,subQ0]});Q2=makeQuery(id+"F0.imprint","IMPRINT",FACE,{"disambiguationData":[TD([[makeQuery(id+"F0.imprint","IMPRINT",EDGE,{"disambiguationData":[TD([[subQ2,-1.0]])],"derivedFrom":subQ1}),-1.0]])]});}
            var Q3;
            {var subQ0=sQuery(id+"F0.wireOp",EDGE,"E37.0");var subQ1=sQuery(id+"F0.wireOp",EDGE,"E24");var subQ2=makeQuery(id+"F0.imprint","INTERSECT",VERTEX,{"derivedFrom":[subQ1,subQ0]});Q3=makeQuery(id+"F0.imprint","IMPRINT",FACE,{"disambiguationData":[TD([[makeQuery(id+"F0.imprint","IMPRINT",EDGE,{"disambiguationData":[TD([[subQ2,-1.0]])],"derivedFrom":subQ1}),-1.0]])]});}
            var Q4;
            {var subQ0=sQuery(id+"F0.wireOp",EDGE,"E39.0");var subQ1=sQuery(id+"F0.wireOp",EDGE,"E24");var subQ2=makeQuery(id+"F0.imprint","INTERSECT",VERTEX,{"derivedFrom":[subQ1,subQ0]});Q4=makeQuery(id+"F0.imprint","IMPRINT",FACE,{"disambiguationData":[TD([[makeQuery(id+"F0.imprint","IMPRINT",EDGE,{"disambiguationData":[TD([[subQ2,-1.0]])],"derivedFrom":subQ1}),-1.0]])]});}
            var Q5;
            {var subQ0=sQuery(id+"F0.wireOp",EDGE,"E43.0");var subQ1=sQuery(id+"F0.wireOp",EDGE,"E24");var subQ2=makeQuery(id+"F0.imprint","INTERSECT",VERTEX,{"derivedFrom":[subQ1,subQ0]});Q5=makeQuery(id+"F0.imprint","IMPRINT",FACE,{"disambiguationData":[TD([[makeQuery(id+"F0.imprint","IMPRINT",EDGE,{"disambiguationData":[TD([[subQ2,-1.0]])],"derivedFrom":subQ1}),-1.0]])]});}
            var Q6;
            {var subQ0=sQuery(id+"F0.wireOp",EDGE,"E30.8.0");var subQ1=sQuery(id+"F0.wireOp",EDGE,"E24");var subQ2=makeQuery(id+"F0.imprint","INTERSECT",VERTEX,{"derivedFrom":[subQ1,subQ0]});Q6=makeQuery(id+"F0.imprint","IMPRINT",FACE,{"disambiguationData":[TD([[makeQuery(id+"F0.imprint","IMPRINT",EDGE,{"disambiguationData":[TD([[subQ2,1.0]])],"derivedFrom":subQ1}),-1.0]])]});}
            var Q7;
            {var subQ0=sQuery(id+"F0.wireOp",EDGE,"E33.0");var subQ1=sQuery(id+"F0.wireOp",EDGE,"E22");var subQ2=makeQuery(id+"F0.imprint","INTERSECT",VERTEX,{"derivedFrom":[subQ1,subQ0]});Q7=makeQuery(id+"F0.imprint","IMPRINT",FACE,{"disambiguationData":[TD([[makeQuery(id+"F0.imprint","IMPRINT",EDGE,{"disambiguationData":[TD([[subQ2,1.0]])],"derivedFrom":subQ1}),-1.0]])]});}
            var Q8;
            {var subQ0=sQuery(id+"F0.wireOp",EDGE,"E31.0");var subQ1=sQuery(id+"F0.wireOp",EDGE,"E22");var subQ2=makeQuery(id+"F0.imprint","INTERSECT",VERTEX,{"derivedFrom":[subQ1,subQ0]});Q8=makeQuery(id+"F0.imprint","IMPRINT",FACE,{"disambiguationData":[TD([[makeQuery(id+"F0.imprint","IMPRINT",EDGE,{"disambiguationData":[TD([[subQ2,1.0]])],"derivedFrom":subQ1}),-1.0]])]});}
            var Q9;
            {var subQ0=sQuery(id+"F0.wireOp",EDGE,"E35.0");var subQ1=sQuery(id+"F0.wireOp",EDGE,"E22");var subQ2=makeQuery(id+"F0.imprint","INTERSECT",VERTEX,{"derivedFrom":[subQ1,subQ0]});Q9=makeQuery(id+"F0.imprint","IMPRINT",FACE,{"disambiguationData":[TD([[makeQuery(id+"F0.imprint","IMPRINT",EDGE,{"disambiguationData":[TD([[subQ2,1.0]])],"derivedFrom":subQ1}),-1.0]])]});}
            var Q10;
            {var subQ0=sQuery(id+"F0.wireOp",EDGE,"E37.0");var subQ1=sQuery(id+"F0.wireOp",EDGE,"E22");var subQ2=makeQuery(id+"F0.imprint","INTERSECT",VERTEX,{"derivedFrom":[subQ1,subQ0]});Q10=makeQuery(id+"F0.imprint","IMPRINT",FACE,{"disambiguationData":[TD([[makeQuery(id+"F0.imprint","IMPRINT",EDGE,{"disambiguationData":[TD([[subQ2,1.0]])],"derivedFrom":subQ1}),-1.0]])]});}
            var Q11;
            {var subQ0=sQuery(id+"F0.wireOp",EDGE,"E39.0");var subQ1=sQuery(id+"F0.wireOp",EDGE,"E22");var subQ2=makeQuery(id+"F0.imprint","INTERSECT",VERTEX,{"derivedFrom":[subQ1,subQ0]});Q11=makeQuery(id+"F0.imprint","IMPRINT",FACE,{"disambiguationData":[TD([[makeQuery(id+"F0.imprint","IMPRINT",EDGE,{"disambiguationData":[TD([[subQ2,1.0]])],"derivedFrom":subQ1}),-1.0]])]});}
            var Q12;
            {var subQ0=sQuery(id+"F0.wireOp",EDGE,"E43.0");var subQ1=sQuery(id+"F0.wireOp",EDGE,"E22");var subQ2=makeQuery(id+"F0.imprint","INTERSECT",VERTEX,{"derivedFrom":[subQ1,subQ0]});Q12=makeQuery(id+"F0.imprint","IMPRINT",FACE,{"disambiguationData":[TD([[makeQuery(id+"F0.imprint","IMPRINT",EDGE,{"disambiguationData":[TD([[subQ2,1.0]])],"derivedFrom":subQ1}),-1.0]])]});}
            var Q13;
            {var subQ0=sQuery(id+"F0.wireOp",EDGE,"E41.0");var subQ1=sQuery(id+"F0.wireOp",EDGE,"E22");var subQ2=makeQuery(id+"F0.imprint","INTERSECT",VERTEX,{"derivedFrom":[subQ1,subQ0]});Q13=makeQuery(id+"F0.imprint","IMPRINT",FACE,{"disambiguationData":[TD([[makeQuery(id+"F0.imprint","IMPRINT",EDGE,{"disambiguationData":[TD([[subQ2,1.0]])],"derivedFrom":subQ1}),-1.0]])]});}
            var Q14;
            {var subQ0=sQuery(id+"F0.wireOp",EDGE,"E42.0");var subQ1=sQuery(id+"F0.wireOp",EDGE,"E24");var subQ2=makeQuery(id+"F0.imprint","INTERSECT",VERTEX,{"derivedFrom":[subQ1,subQ0]});Q14=makeQuery(id+"F0.imprint","IMPRINT",FACE,{"disambiguationData":[TD([[makeQuery(id+"F0.imprint","IMPRINT",EDGE,{"disambiguationData":[TD([[subQ2,-1.0]])],"derivedFrom":subQ1}),-1.0]])]});}
            var Q15;
            {var subQ0=sQuery(id+"F0.wireOp",EDGE,"E44.0");var subQ1=sQuery(id+"F0.wireOp",EDGE,"E24");var subQ2=makeQuery(id+"F0.imprint","INTERSECT",VERTEX,{"derivedFrom":[subQ1,subQ0]});Q15=makeQuery(id+"F0.imprint","IMPRINT",FACE,{"disambiguationData":[TD([[makeQuery(id+"F0.imprint","IMPRINT",EDGE,{"disambiguationData":[TD([[subQ2,-1.0]])],"derivedFrom":subQ1}),-1.0]])]});}
            var Q16;
            {var subQ0=sQuery(id+"F0.wireOp",EDGE,"E40.0");var subQ1=sQuery(id+"F0.wireOp",EDGE,"E24");var subQ2=makeQuery(id+"F0.imprint","INTERSECT",VERTEX,{"derivedFrom":[subQ1,subQ0]});Q16=makeQuery(id+"F0.imprint","IMPRINT",FACE,{"disambiguationData":[TD([[makeQuery(id+"F0.imprint","IMPRINT",EDGE,{"disambiguationData":[TD([[subQ2,-1.0]])],"derivedFrom":subQ1}),-1.0]])]});}
            var Q17;
            {var subQ0=sQuery(id+"F0.wireOp",EDGE,"E38.0");var subQ1=sQuery(id+"F0.wireOp",EDGE,"E24");var subQ2=makeQuery(id+"F0.imprint","INTERSECT",VERTEX,{"derivedFrom":[subQ1,subQ0]});Q17=makeQuery(id+"F0.imprint","IMPRINT",FACE,{"disambiguationData":[TD([[makeQuery(id+"F0.imprint","IMPRINT",EDGE,{"disambiguationData":[TD([[subQ2,-1.0]])],"derivedFrom":subQ1}),-1.0]])]});}
            var Q18;
            {var subQ0=sQuery(id+"F0.wireOp",EDGE,"E36.MirrorCS");var subQ1=sQuery(id+"F0.wireOp",EDGE,"E24");var subQ2=makeQuery(id+"F0.imprint","INTERSECT",VERTEX,{"derivedFrom":[subQ1,subQ0]});Q18=makeQuery(id+"F0.imprint","IMPRINT",FACE,{"disambiguationData":[TD([[makeQuery(id+"F0.imprint","IMPRINT",EDGE,{"disambiguationData":[TD([[subQ2,-1.0]])],"derivedFrom":subQ1}),-1.0]])]});}
            var Q19;
            {var subQ0=sQuery(id+"F0.wireOp",EDGE,"E34.MirrorCS");var subQ1=sQuery(id+"F0.wireOp",EDGE,"E24");var subQ2=makeQuery(id+"F0.imprint","INTERSECT",VERTEX,{"derivedFrom":[subQ1,subQ0]});Q19=makeQuery(id+"F0.imprint","IMPRINT",FACE,{"disambiguationData":[TD([[makeQuery(id+"F0.imprint","IMPRINT",EDGE,{"disambiguationData":[TD([[subQ2,-1.0]])],"derivedFrom":subQ1}),-1.0]])]});}
            var Q20;
            {var subQ0=sQuery(id+"F0.wireOp",EDGE,"E32.MirrorCS");var subQ1=sQuery(id+"F0.wireOp",EDGE,"E24");var subQ2=makeQuery(id+"F0.imprint","INTERSECT",VERTEX,{"derivedFrom":[subQ1,subQ0]});Q20=makeQuery(id+"F0.imprint","IMPRINT",FACE,{"disambiguationData":[TD([[makeQuery(id+"F0.imprint","IMPRINT",EDGE,{"disambiguationData":[TD([[subQ2,-1.0]])],"derivedFrom":subQ1}),-1.0]])]});}
            var Q21;
            {var subQ0=sQuery(id+"F0.wireOp",EDGE,"E32.MirrorCS");var subQ1=sQuery(id+"F0.wireOp",EDGE,"E25");var subQ2=makeQuery(id+"F0.imprint","INTERSECT",VERTEX,{"derivedFrom":[subQ1,subQ0]});Q21=makeQuery(id+"F0.imprint","IMPRINT",FACE,{"disambiguationData":[TD([[makeQuery(id+"F0.imprint","IMPRINT",EDGE,{"disambiguationData":[TD([[subQ2,-1.0]])],"derivedFrom":subQ1}),-1.0]])]});}
            var Q22;
            {var subQ0=sQuery(id+"F0.wireOp",EDGE,"E34.MirrorCS");var subQ1=sQuery(id+"F0.wireOp",EDGE,"E25");var subQ2=makeQuery(id+"F0.imprint","INTERSECT",VERTEX,{"derivedFrom":[subQ1,subQ0]});Q22=makeQuery(id+"F0.imprint","IMPRINT",FACE,{"disambiguationData":[TD([[makeQuery(id+"F0.imprint","IMPRINT",EDGE,{"disambiguationData":[TD([[subQ2,-1.0]])],"derivedFrom":subQ1}),-1.0]])]});}
            var Q23;
            {var subQ0=sQuery(id+"F0.wireOp",EDGE,"E36.MirrorCS");var subQ1=sQuery(id+"F0.wireOp",EDGE,"E25");var subQ2=makeQuery(id+"F0.imprint","INTERSECT",VERTEX,{"derivedFrom":[subQ1,subQ0]});Q23=makeQuery(id+"F0.imprint","IMPRINT",FACE,{"disambiguationData":[TD([[makeQuery(id+"F0.imprint","IMPRINT",EDGE,{"disambiguationData":[TD([[subQ2,-1.0]])],"derivedFrom":subQ1}),-1.0]])]});}
            var Q24;
            {var subQ0=sQuery(id+"F0.wireOp",EDGE,"E38.0");var subQ1=sQuery(id+"F0.wireOp",EDGE,"E25");var subQ2=makeQuery(id+"F0.imprint","INTERSECT",VERTEX,{"derivedFrom":[subQ1,subQ0]});Q24=makeQuery(id+"F0.imprint","IMPRINT",FACE,{"disambiguationData":[TD([[makeQuery(id+"F0.imprint","IMPRINT",EDGE,{"disambiguationData":[TD([[subQ2,-1.0]])],"derivedFrom":subQ1}),-1.0]])]});}
            var Q25;
            {var subQ0=sQuery(id+"F0.wireOp",EDGE,"E40.0");var subQ1=sQuery(id+"F0.wireOp",EDGE,"E25");var subQ2=makeQuery(id+"F0.imprint","INTERSECT",VERTEX,{"derivedFrom":[subQ1,subQ0]});Q25=makeQuery(id+"F0.imprint","IMPRINT",FACE,{"disambiguationData":[TD([[makeQuery(id+"F0.imprint","IMPRINT",EDGE,{"disambiguationData":[TD([[subQ2,-1.0]])],"derivedFrom":subQ1}),-1.0]])]});}
            var Q26;
            {var subQ0=sQuery(id+"F0.wireOp",EDGE,"E44.0");var subQ1=sQuery(id+"F0.wireOp",EDGE,"E25");var subQ2=makeQuery(id+"F0.imprint","INTERSECT",VERTEX,{"derivedFrom":[subQ1,subQ0]});Q26=makeQuery(id+"F0.imprint","IMPRINT",FACE,{"disambiguationData":[TD([[makeQuery(id+"F0.imprint","IMPRINT",EDGE,{"disambiguationData":[TD([[subQ2,-1.0]])],"derivedFrom":subQ1}),-1.0]])]});}
            var Q27;
            {var subQ0=sQuery(id+"F0.wireOp",EDGE,"E42.0");var subQ1=sQuery(id+"F0.wireOp",EDGE,"E25");var subQ2=makeQuery(id+"F0.imprint","INTERSECT",VERTEX,{"derivedFrom":[subQ1,subQ0]});Q27=makeQuery(id+"F0.imprint","IMPRINT",FACE,{"disambiguationData":[TD([[makeQuery(id+"F0.imprint","IMPRINT",EDGE,{"disambiguationData":[TD([[subQ2,-1.0]])],"derivedFrom":subQ1}),-1.0]])]});}
            var Q28;
            {var subQ0=sQuery(id+"F0.wireOp",EDGE,"E30.8.0");var subQ1=sQuery(id+"F0.wireOp",EDGE,"E26");var subQ2=makeQuery(id+"F0.imprint","INTERSECT",VERTEX,{"derivedFrom":[subQ1,subQ0]});Q28=makeQuery(id+"F0.imprint","IMPRINT",FACE,{"disambiguationData":[TD([[makeQuery(id+"F0.imprint","IMPRINT",EDGE,{"disambiguationData":[TD([[subQ2,1.0]])],"derivedFrom":subQ1}),-1.0]])]});}
            var Q29;
            {var subQ0=sQuery(id+"F0.wireOp",EDGE,"E42.0");var subQ1=sQuery(id+"F0.wireOp",EDGE,"E26");var subQ2=makeQuery(id+"F0.imprint","INTERSECT",VERTEX,{"derivedFrom":[subQ1,subQ0]});Q29=makeQuery(id+"F0.imprint","IMPRINT",FACE,{"disambiguationData":[TD([[makeQuery(id+"F0.imprint","IMPRINT",EDGE,{"disambiguationData":[TD([[subQ2,-1.0]])],"derivedFrom":subQ1}),-1.0]])]});}
            var Q30;
            {var subQ0=sQuery(id+"F0.wireOp",EDGE,"E43.0");var subQ1=sQuery(id+"F0.wireOp",EDGE,"E26");var subQ2=makeQuery(id+"F0.imprint","INTERSECT",VERTEX,{"derivedFrom":[subQ1,subQ0]});Q30=makeQuery(id+"F0.imprint","IMPRINT",FACE,{"disambiguationData":[TD([[makeQuery(id+"F0.imprint","IMPRINT",EDGE,{"disambiguationData":[TD([[subQ2,-1.0]])],"derivedFrom":subQ1}),-1.0]])]});}
            var Q31;
            {var subQ0=sQuery(id+"F0.wireOp",EDGE,"E44.0");var subQ1=sQuery(id+"F0.wireOp",EDGE,"E26");var subQ2=makeQuery(id+"F0.imprint","INTERSECT",VERTEX,{"derivedFrom":[subQ1,subQ0]});Q31=makeQuery(id+"F0.imprint","IMPRINT",FACE,{"disambiguationData":[TD([[makeQuery(id+"F0.imprint","IMPRINT",EDGE,{"disambiguationData":[TD([[subQ2,-1.0]])],"derivedFrom":subQ1}),-1.0]])]});}
            var Q32;
            {var subQ0=sQuery(id+"F0.wireOp",EDGE,"E39.0");var subQ1=sQuery(id+"F0.wireOp",EDGE,"E26");var subQ2=makeQuery(id+"F0.imprint","INTERSECT",VERTEX,{"derivedFrom":[subQ1,subQ0]});Q32=makeQuery(id+"F0.imprint","IMPRINT",FACE,{"disambiguationData":[TD([[makeQuery(id+"F0.imprint","IMPRINT",EDGE,{"disambiguationData":[TD([[subQ2,-1.0]])],"derivedFrom":subQ1}),-1.0]])]});}
            var Q33;
            {var subQ0=sQuery(id+"F0.wireOp",EDGE,"E40.0");var subQ1=sQuery(id+"F0.wireOp",EDGE,"E26");var subQ2=makeQuery(id+"F0.imprint","INTERSECT",VERTEX,{"derivedFrom":[subQ1,subQ0]});Q33=makeQuery(id+"F0.imprint","IMPRINT",FACE,{"disambiguationData":[TD([[makeQuery(id+"F0.imprint","IMPRINT",EDGE,{"disambiguationData":[TD([[subQ2,-1.0]])],"derivedFrom":subQ1}),-1.0]])]});}
            var Q34;
            {var subQ0=sQuery(id+"F0.wireOp",EDGE,"E37.0");var subQ1=sQuery(id+"F0.wireOp",EDGE,"E26");var subQ2=makeQuery(id+"F0.imprint","INTERSECT",VERTEX,{"derivedFrom":[subQ1,subQ0]});Q34=makeQuery(id+"F0.imprint","IMPRINT",FACE,{"disambiguationData":[TD([[makeQuery(id+"F0.imprint","IMPRINT",EDGE,{"disambiguationData":[TD([[subQ2,-1.0]])],"derivedFrom":subQ1}),-1.0]])]});}
            var Q35;
            {var subQ0=sQuery(id+"F0.wireOp",EDGE,"E38.0");var subQ1=sQuery(id+"F0.wireOp",EDGE,"E26");var subQ2=makeQuery(id+"F0.imprint","INTERSECT",VERTEX,{"derivedFrom":[subQ1,subQ0]});Q35=makeQuery(id+"F0.imprint","IMPRINT",FACE,{"disambiguationData":[TD([[makeQuery(id+"F0.imprint","IMPRINT",EDGE,{"disambiguationData":[TD([[subQ2,-1.0]])],"derivedFrom":subQ1}),-1.0]])]});}
            var Q36;
            {var subQ0=sQuery(id+"F0.wireOp",EDGE,"E35.0");var subQ1=sQuery(id+"F0.wireOp",EDGE,"E26");var subQ2=makeQuery(id+"F0.imprint","INTERSECT",VERTEX,{"derivedFrom":[subQ1,subQ0]});Q36=makeQuery(id+"F0.imprint","IMPRINT",FACE,{"disambiguationData":[TD([[makeQuery(id+"F0.imprint","IMPRINT",EDGE,{"disambiguationData":[TD([[subQ2,-1.0]])],"derivedFrom":subQ1}),-1.0]])]});}
            var Q37;
            {var subQ0=sQuery(id+"F0.wireOp",EDGE,"E36.MirrorCS");var subQ1=sQuery(id+"F0.wireOp",EDGE,"E26");var subQ2=makeQuery(id+"F0.imprint","INTERSECT",VERTEX,{"derivedFrom":[subQ1,subQ0]});Q37=makeQuery(id+"F0.imprint","IMPRINT",FACE,{"disambiguationData":[TD([[makeQuery(id+"F0.imprint","IMPRINT",EDGE,{"disambiguationData":[TD([[subQ2,-1.0]])],"derivedFrom":subQ1}),-1.0]])]});}
            var Q38;
            {var subQ0=sQuery(id+"F0.wireOp",EDGE,"E33.0");var subQ1=sQuery(id+"F0.wireOp",EDGE,"E26");var subQ2=makeQuery(id+"F0.imprint","INTERSECT",VERTEX,{"derivedFrom":[subQ1,subQ0]});Q38=makeQuery(id+"F0.imprint","IMPRINT",FACE,{"disambiguationData":[TD([[makeQuery(id+"F0.imprint","IMPRINT",EDGE,{"disambiguationData":[TD([[subQ2,-1.0]])],"derivedFrom":subQ1}),-1.0]])]});}
            var Q39;
            {var subQ0=sQuery(id+"F0.wireOp",EDGE,"E34.MirrorCS");var subQ1=sQuery(id+"F0.wireOp",EDGE,"E26");var subQ2=makeQuery(id+"F0.imprint","INTERSECT",VERTEX,{"derivedFrom":[subQ1,subQ0]});Q39=makeQuery(id+"F0.imprint","IMPRINT",FACE,{"disambiguationData":[TD([[makeQuery(id+"F0.imprint","IMPRINT",EDGE,{"disambiguationData":[TD([[subQ2,-1.0]])],"derivedFrom":subQ1}),-1.0]])]});}
            var Q40;
            {var subQ0=sQuery(id+"F0.wireOp",EDGE,"E31.0");var subQ1=sQuery(id+"F0.wireOp",EDGE,"E26");var subQ2=makeQuery(id+"F0.imprint","INTERSECT",VERTEX,{"derivedFrom":[subQ1,subQ0]});Q40=makeQuery(id+"F0.imprint","IMPRINT",FACE,{"disambiguationData":[TD([[makeQuery(id+"F0.imprint","IMPRINT",EDGE,{"disambiguationData":[TD([[subQ2,-1.0]])],"derivedFrom":subQ1}),-1.0]])]});}
            var Q41;
            {var subQ0=sQuery(id+"F0.wireOp",EDGE,"E32.MirrorCS");var subQ1=sQuery(id+"F0.wireOp",EDGE,"E26");var subQ2=makeQuery(id+"F0.imprint","INTERSECT",VERTEX,{"derivedFrom":[subQ1,subQ0]});Q41=makeQuery(id+"F0.imprint","IMPRINT",FACE,{"disambiguationData":[TD([[makeQuery(id+"F0.imprint","IMPRINT",EDGE,{"disambiguationData":[TD([[subQ2,-1.0]])],"derivedFrom":subQ1}),-1.0]])]});}
            var Q42;
            {var subQ0=sQuery(id+"F0.wireOp",EDGE,"E29");var subQ1=sQuery(id+"F0.wireOp",EDGE,"E26");var subQ2=makeQuery(id+"F0.imprint","INTERSECT",VERTEX,{"derivedFrom":[subQ1,subQ0]});Q42=makeQuery(id+"F0.imprint","IMPRINT",FACE,{"disambiguationData":[TD([[makeQuery(id+"F0.imprint","IMPRINT",EDGE,{"disambiguationData":[TD([[subQ2,-1.0]])],"derivedFrom":subQ1}),-1.0]])]});}
            var Q43;
            {var subQ13=sQuery(id+"F0.wireOp",EDGE,"E28");Q43=makeQuery(id+"F0.imprint","IMPRINT",FACE,{"disambiguationData":[TD([[makeQuery(id+"F0.imprint","IMPRINT",EDGE,{"derivedFrom":subQ13}),1.0]])]});}
            var Q44;
            {var subQ3=sQuery(id+"F0.wireOp",EDGE,"E34.MirrorCS");var subQ7=sQuery(id+"F0.wireOp",EDGE,"E27");var subQ9=makeQuery(id+"F0.imprint","INTERSECT",VERTEX,{"derivedFrom":[subQ7,subQ3]});Q44=makeQuery(id+"F0.imprint","IMPRINT",FACE,{"disambiguationData":[TD([[makeQuery(id+"F0.imprint","IMPRINT",EDGE,{"disambiguationData":[TD([[subQ9,-1.0]])],"derivedFrom":subQ7}),-1.0]])]});}
            var Q45;
            {var subQ0=sQuery(id+"F0.wireOp",EDGE,"E38.0");var subQ3=sQuery(id+"F0.wireOp",EDGE,"E27");var subQ4=makeQuery(id+"F0.imprint","INTERSECT",VERTEX,{"derivedFrom":[subQ3,subQ0]});Q45=makeQuery(id+"F0.imprint","IMPRINT",FACE,{"disambiguationData":[TD([[makeQuery(id+"F0.imprint","IMPRINT",EDGE,{"disambiguationData":[TD([[subQ4,-1.0]])],"derivedFrom":subQ3}),-1.0]])]});}
            var Q46;
            {var subQ0=sQuery(id+"F0.wireOp",EDGE,"E33.0");var subQ1=sQuery(id+"F0.wireOp",EDGE,"E24");var subQ2=makeQuery(id+"F0.imprint","INTERSECT",VERTEX,{"derivedFrom":[subQ1,subQ0]});Q46=makeQuery(id+"F0.imprint","IMPRINT",FACE,{"disambiguationData":[TD([[makeQuery(id+"F0.imprint","IMPRINT",EDGE,{"disambiguationData":[TD([[subQ2,-1.0]])],"derivedFrom":subQ1}),-1.0]])]});}
            extrude(context, id + "F2", {"entities" : qUnion([Q0, Q1, Q2, Q3, Q4, Q5, Q6, Q7, Q8, Q9, Q10, Q11, Q12, Q13, Q14, Q15, Q16, Q17, Q18, Q19, Q20, Q21, Q22, Q23, Q24, Q25, Q26, Q27, Q28, Q29, Q30, Q31, Q32, Q33, Q34, Q35, Q36, Q37, Q38, Q39, Q40, Q41, Q42, Q43, Q44, Q45, Q46]), "operationType" : NewBodyOperationType.ADD, "depth" : 1.5 * mm});
        }
        {
            var Q0;
            {var subQ31=sQuery(id+"F0.wireOp",EDGE,"E13.right");Q0=makeQuery(id+"F0.imprint","IMPRINT",FACE,{"disambiguationData":[TD([[makeQuery(id+"F0.imprint","IMPRINT",EDGE,{"derivedFrom":subQ31}),1.0]])]});}
            extrude(context, id + "F3", {"entities" : qUnion([Q0]), "operationType" : NewBodyOperationType.ADD, "depth" : 2 * mm});
        }
        {
            var Q0;
            Q0=makeQuery(id+"F3.opExtrude","CAP_EDGE",EDGE,{"disambiguationData":[OSD([sQuery(id+"F0.wireOp",EDGE,"E18.4.5.4")])],"isStart":false});
            var Q1;
            Q1=makeQuery(id+"F3.opExtrude","CAP_EDGE",EDGE,{"disambiguationData":[OSD([sQuery(id+"F0.wireOp",EDGE,"E18.4.5.3")])],"isStart":false});
            var Q2;
            Q2=makeQuery(id+"F3.opExtrude","CAP_EDGE",EDGE,{"disambiguationData":[OSD([sQuery(id+"F0.wireOp",EDGE,"E18.3.5.4")])],"isStart":false});
            var Q3;
            Q3=makeQuery(id+"F3.opExtrude","CAP_EDGE",EDGE,{"disambiguationData":[OSD([sQuery(id+"F0.wireOp",EDGE,"E18.3.5.3")])],"isStart":false});
            var Q4;
            Q4=makeQuery(id+"F3.opExtrude","CAP_EDGE",EDGE,{"disambiguationData":[OSD([sQuery(id+"F0.wireOp",EDGE,"E18.2.5.4")])],"isStart":false});
            var Q5;
            Q5=makeQuery(id+"F3.opExtrude","CAP_EDGE",EDGE,{"disambiguationData":[OSD([sQuery(id+"F0.wireOp",EDGE,"E18.2.5.3")])],"isStart":false});
            var Q6;
            Q6=makeQuery(id+"F3.opExtrude","CAP_EDGE",EDGE,{"disambiguationData":[OSD([sQuery(id+"F0.wireOp",EDGE,"E18.1.5.4")])],"isStart":false});
            var Q7;
            Q7=makeQuery(id+"F3.opExtrude","CAP_EDGE",EDGE,{"disambiguationData":[OSD([sQuery(id+"F0.wireOp",EDGE,"E18.1.5.3")])],"isStart":false});
            var Q8;
            Q8=makeQuery(id+"F3.opExtrude","CAP_EDGE",EDGE,{"disambiguationData":[OSD([sQuery(id+"F0.wireOp",EDGE,"E18.1.4.1")])],"isStart":false});
            var Q9;
            Q9=makeQuery(id+"F3.opExtrude","CAP_EDGE",EDGE,{"disambiguationData":[OSD([sQuery(id+"F0.wireOp",EDGE,"E18.1.4.2")])],"isStart":false});
            var Q10;
            Q10=makeQuery(id+"F3.opExtrude","CAP_EDGE",EDGE,{"disambiguationData":[OSD([sQuery(id+"F0.wireOp",EDGE,"E18.1.4.3")])],"isStart":false});
            var Q11;
            Q11=makeQuery(id+"F3.opExtrude","CAP_EDGE",EDGE,{"disambiguationData":[OSD([sQuery(id+"F0.wireOp",EDGE,"E18.1.4.4")])],"isStart":false});
            var Q12;
            Q12=makeQuery(id+"F3.opExtrude","CAP_EDGE",EDGE,{"disambiguationData":[OSD([sQuery(id+"F0.wireOp",EDGE,"E18.2.4.2")])],"isStart":false});
            var Q13;
            Q13=makeQuery(id+"F3.opExtrude","CAP_EDGE",EDGE,{"disambiguationData":[OSD([sQuery(id+"F0.wireOp",EDGE,"E18.2.4.1")])],"isStart":false});
            var Q14;
            Q14=makeQuery(id+"F3.opExtrude","CAP_EDGE",EDGE,{"disambiguationData":[OSD([sQuery(id+"F0.wireOp",EDGE,"E18.3.4.2")])],"isStart":false});
            var Q15;
            Q15=makeQuery(id+"F3.opExtrude","CAP_EDGE",EDGE,{"disambiguationData":[OSD([sQuery(id+"F0.wireOp",EDGE,"E18.3.4.1")])],"isStart":false});
            var Q16;
            Q16=makeQuery(id+"F3.opExtrude","CAP_EDGE",EDGE,{"disambiguationData":[OSD([sQuery(id+"F0.wireOp",EDGE,"E18.4.4.1")])],"isStart":false});
            var Q17;
            Q17=makeQuery(id+"F3.opExtrude","CAP_EDGE",EDGE,{"disambiguationData":[OSD([sQuery(id+"F0.wireOp",EDGE,"E18.4.4.2")])],"isStart":false});
            var Q18;
            Q18=makeQuery(id+"F3.opExtrude","CAP_EDGE",EDGE,{"disambiguationData":[OSD([sQuery(id+"F0.wireOp",EDGE,"E18.5.4.1")])],"isStart":false});
            var Q19;
            Q19=makeQuery(id+"F3.opExtrude","CAP_EDGE",EDGE,{"disambiguationData":[OSD([sQuery(id+"F0.wireOp",EDGE,"E18.5.4.2")])],"isStart":false});
            var Q20;
            Q20=makeQuery(id+"F3.opExtrude","CAP_EDGE",EDGE,{"disambiguationData":[OSD([sQuery(id+"F0.wireOp",EDGE,"E18.4.4.4")])],"isStart":false});
            var Q21;
            Q21=makeQuery(id+"F3.opExtrude","CAP_EDGE",EDGE,{"disambiguationData":[OSD([sQuery(id+"F0.wireOp",EDGE,"E18.4.4.3")])],"isStart":false});
            var Q22;
            Q22=makeQuery(id+"F3.opExtrude","CAP_EDGE",EDGE,{"disambiguationData":[OSD([sQuery(id+"F0.wireOp",EDGE,"E18.4.3.4")])],"isStart":false});
            var Q23;
            Q23=makeQuery(id+"F3.opExtrude","CAP_EDGE",EDGE,{"disambiguationData":[OSD([sQuery(id+"F0.wireOp",EDGE,"E18.4.3.3")])],"isStart":false});
            var Q24;
            Q24=makeQuery(id+"F3.opExtrude","CAP_EDGE",EDGE,{"disambiguationData":[OSD([sQuery(id+"F0.wireOp",EDGE,"E18.3.3.4")])],"isStart":false});
            var Q25;
            Q25=makeQuery(id+"F3.opExtrude","CAP_EDGE",EDGE,{"disambiguationData":[OSD([sQuery(id+"F0.wireOp",EDGE,"E18.3.4.4")])],"isStart":false});
            var Q26;
            Q26=makeQuery(id+"F3.opExtrude","CAP_EDGE",EDGE,{"disambiguationData":[OSD([sQuery(id+"F0.wireOp",EDGE,"E18.3.4.3")])],"isStart":false});
            var Q27;
            Q27=makeQuery(id+"F3.opExtrude","CAP_EDGE",EDGE,{"disambiguationData":[OSD([sQuery(id+"F0.wireOp",EDGE,"E18.2.4.4")])],"isStart":false});
            var Q28;
            Q28=makeQuery(id+"F3.opExtrude","CAP_EDGE",EDGE,{"disambiguationData":[OSD([sQuery(id+"F0.wireOp",EDGE,"E18.2.4.3")])],"isStart":false});
            var Q29;
            Q29=makeQuery(id+"F3.opExtrude","CAP_EDGE",EDGE,{"disambiguationData":[OSD([sQuery(id+"F0.wireOp",EDGE,"E18.2.3.4")])],"isStart":false});
            var Q30;
            Q30=makeQuery(id+"F3.opExtrude","CAP_EDGE",EDGE,{"disambiguationData":[OSD([sQuery(id+"F0.wireOp",EDGE,"E18.2.3.3")])],"isStart":false});
            var Q31;
            Q31=makeQuery(id+"F3.opExtrude","CAP_EDGE",EDGE,{"disambiguationData":[OSD([sQuery(id+"F0.wireOp",EDGE,"E18.1.3.4")])],"isStart":false});
            var Q32;
            Q32=makeQuery(id+"F3.opExtrude","CAP_EDGE",EDGE,{"disambiguationData":[OSD([sQuery(id+"F0.wireOp",EDGE,"E18.1.3.3")])],"isStart":false});
            var Q33;
            Q33=makeQuery(id+"F3.opExtrude","CAP_EDGE",EDGE,{"disambiguationData":[OSD([sQuery(id+"F0.wireOp",EDGE,"E18.0.3.4")])],"isStart":false});
            var Q34;
            Q34=makeQuery(id+"F3.opExtrude","CAP_EDGE",EDGE,{"disambiguationData":[OSD([sQuery(id+"F0.wireOp",EDGE,"E18.0.3.3")])],"isStart":false});
            var Q35;
            Q35=makeQuery(id+"F3.opExtrude","CAP_EDGE",EDGE,{"disambiguationData":[OSD([sQuery(id+"F0.wireOp",EDGE,"E18.0.4.4")])],"isStart":false});
            var Q36;
            Q36=makeQuery(id+"F3.opExtrude","CAP_EDGE",EDGE,{"disambiguationData":[OSD([sQuery(id+"F0.wireOp",EDGE,"E18.0.4.3")])],"isStart":false});
            var Q37;
            Q37=makeQuery(id+"F3.opExtrude","CAP_EDGE",EDGE,{"disambiguationData":[OSD([sQuery(id+"F0.wireOp",EDGE,"E18.0.5.4")])],"isStart":false});
            var Q38;
            Q38=makeQuery(id+"F3.opExtrude","CAP_EDGE",EDGE,{"disambiguationData":[OSD([sQuery(id+"F0.wireOp",EDGE,"E18.0.5.3")])],"isStart":false});
            var Q39;
            Q39=makeQuery(id+"F3.opExtrude","CAP_EDGE",EDGE,{"disambiguationData":[OSD([sQuery(id+"F0.wireOp",EDGE,"E18.0.4.1")])],"isStart":false});
            var Q40;
            Q40=makeQuery(id+"F3.opExtrude","CAP_EDGE",EDGE,{"disambiguationData":[OSD([sQuery(id+"F0.wireOp",EDGE,"E18.0.4.2")])],"isStart":false});
            var Q41;
            Q41=makeQuery(id+"F3.opExtrude","CAP_EDGE",EDGE,{"disambiguationData":[OSD([sQuery(id+"F0.wireOp",EDGE,"E18.0.3.2")])],"isStart":false});
            var Q42;
            Q42=makeQuery(id+"F3.opExtrude","CAP_EDGE",EDGE,{"disambiguationData":[OSD([sQuery(id+"F0.wireOp",EDGE,"E18.0.3.1")])],"isStart":false});
            var Q43;
            Q43=makeQuery(id+"F3.opExtrude","CAP_EDGE",EDGE,{"disambiguationData":[OSD([sQuery(id+"F0.wireOp",EDGE,"E18.1.3.2")])],"isStart":false});
            var Q44;
            Q44=makeQuery(id+"F3.opExtrude","CAP_EDGE",EDGE,{"disambiguationData":[OSD([sQuery(id+"F0.wireOp",EDGE,"E18.1.3.1")])],"isStart":false});
            var Q45;
            Q45=makeQuery(id+"F3.opExtrude","CAP_EDGE",EDGE,{"disambiguationData":[OSD([sQuery(id+"F0.wireOp",EDGE,"E18.2.3.2")])],"isStart":false});
            var Q46;
            Q46=makeQuery(id+"F3.opExtrude","CAP_EDGE",EDGE,{"disambiguationData":[OSD([sQuery(id+"F0.wireOp",EDGE,"E18.2.3.1")])],"isStart":false});
            var Q47;
            Q47=makeQuery(id+"F3.opExtrude","CAP_EDGE",EDGE,{"disambiguationData":[OSD([sQuery(id+"F0.wireOp",EDGE,"E18.3.3.2")])],"isStart":false});
            var Q48;
            Q48=makeQuery(id+"F3.opExtrude","CAP_EDGE",EDGE,{"disambiguationData":[OSD([sQuery(id+"F0.wireOp",EDGE,"E18.3.3.1")])],"isStart":false});
            var Q49;
            Q49=makeQuery(id+"F3.opExtrude","CAP_EDGE",EDGE,{"disambiguationData":[OSD([sQuery(id+"F0.wireOp",EDGE,"E18.4.3.2")])],"isStart":false});
            var Q50;
            Q50=makeQuery(id+"F3.opExtrude","CAP_EDGE",EDGE,{"disambiguationData":[OSD([sQuery(id+"F0.wireOp",EDGE,"E18.4.3.1")])],"isStart":false});
            var Q51;
            Q51=makeQuery(id+"F3.opExtrude","CAP_EDGE",EDGE,{"disambiguationData":[OSD([sQuery(id+"F0.wireOp",EDGE,"E18.3.3.3")])],"isStart":false});
            var Q52;
            Q52=makeQuery(id+"F3.opExtrude","CAP_EDGE",EDGE,{"disambiguationData":[OSD([sQuery(id+"F0.wireOp",EDGE,"E18.5.3.1")])],"isStart":false});
            var Q53;
            Q53=makeQuery(id+"F3.opExtrude","CAP_EDGE",EDGE,{"disambiguationData":[OSD([sQuery(id+"F0.wireOp",EDGE,"E18.5.3.2")])],"isStart":false});
            var Q54;
            Q54=makeQuery(id+"F3.opExtrude","CAP_EDGE",EDGE,{"disambiguationData":[OSD([sQuery(id+"F0.wireOp",EDGE,"E18.5.2.1")])],"isStart":false});
            var Q55;
            Q55=makeQuery(id+"F3.opExtrude","CAP_EDGE",EDGE,{"disambiguationData":[OSD([sQuery(id+"F0.wireOp",EDGE,"E18.5.2.2")])],"isStart":false});
            var Q56;
            Q56=makeQuery(id+"F3.opExtrude","CAP_EDGE",EDGE,{"disambiguationData":[OSD([sQuery(id+"F0.wireOp",EDGE,"E18.4.2.4")])],"isStart":false});
            var Q57;
            Q57=makeQuery(id+"F3.opExtrude","CAP_EDGE",EDGE,{"disambiguationData":[OSD([sQuery(id+"F0.wireOp",EDGE,"E18.4.2.3")])],"isStart":false});
            var Q58;
            Q58=makeQuery(id+"F3.opExtrude","CAP_EDGE",EDGE,{"disambiguationData":[OSD([sQuery(id+"F0.wireOp",EDGE,"E18.4.2.1")])],"isStart":false});
            var Q59;
            Q59=makeQuery(id+"F3.opExtrude","CAP_EDGE",EDGE,{"disambiguationData":[OSD([sQuery(id+"F0.wireOp",EDGE,"E18.4.2.2")])],"isStart":false});
            var Q60;
            Q60=makeQuery(id+"F3.opExtrude","CAP_EDGE",EDGE,{"disambiguationData":[OSD([sQuery(id+"F0.wireOp",EDGE,"E18.3.2.1")])],"isStart":false});
            var Q61;
            Q61=makeQuery(id+"F3.opExtrude","CAP_EDGE",EDGE,{"disambiguationData":[OSD([sQuery(id+"F0.wireOp",EDGE,"E18.3.2.2")])],"isStart":false});
            var Q62;
            Q62=makeQuery(id+"F3.opExtrude","CAP_EDGE",EDGE,{"disambiguationData":[OSD([sQuery(id+"F0.wireOp",EDGE,"E18.2.2.1")])],"isStart":false});
            var Q63;
            Q63=makeQuery(id+"F3.opExtrude","CAP_EDGE",EDGE,{"disambiguationData":[OSD([sQuery(id+"F0.wireOp",EDGE,"E18.2.2.2")])],"isStart":false});
            var Q64;
            Q64=makeQuery(id+"F3.opExtrude","CAP_EDGE",EDGE,{"disambiguationData":[OSD([sQuery(id+"F0.wireOp",EDGE,"E18.1.2.1")])],"isStart":false});
            var Q65;
            Q65=makeQuery(id+"F3.opExtrude","CAP_EDGE",EDGE,{"disambiguationData":[OSD([sQuery(id+"F0.wireOp",EDGE,"E18.1.2.2")])],"isStart":false});
            var Q66;
            Q66=makeQuery(id+"F3.opExtrude","CAP_EDGE",EDGE,{"disambiguationData":[OSD([sQuery(id+"F0.wireOp",EDGE,"E18.0.2.1")])],"isStart":false});
            var Q67;
            Q67=makeQuery(id+"F3.opExtrude","CAP_EDGE",EDGE,{"disambiguationData":[OSD([sQuery(id+"F0.wireOp",EDGE,"E18.0.2.2")])],"isStart":false});
            var Q68;
            Q68=makeQuery(id+"F3.opExtrude","CAP_EDGE",EDGE,{"disambiguationData":[OSD([sQuery(id+"F0.wireOp",EDGE,"E18.0.2.3")])],"isStart":false});
            var Q69;
            Q69=makeQuery(id+"F3.opExtrude","CAP_EDGE",EDGE,{"disambiguationData":[OSD([sQuery(id+"F0.wireOp",EDGE,"E18.0.2.4")])],"isStart":false});
            var Q70;
            Q70=makeQuery(id+"F3.opExtrude","CAP_EDGE",EDGE,{"disambiguationData":[OSD([sQuery(id+"F0.wireOp",EDGE,"E18.0.1.1")])],"isStart":false});
            var Q71;
            Q71=makeQuery(id+"F3.opExtrude","CAP_EDGE",EDGE,{"disambiguationData":[OSD([sQuery(id+"F0.wireOp",EDGE,"E18.0.1.2")])],"isStart":false});
            var Q72;
            Q72=makeQuery(id+"F3.opExtrude","CAP_EDGE",EDGE,{"disambiguationData":[OSD([sQuery(id+"F0.wireOp",EDGE,"E15.top")])],"isStart":false});
            var Q73;
            Q73=makeQuery(id+"F3.opExtrude","CAP_EDGE",EDGE,{"disambiguationData":[OSD([sQuery(id+"F0.wireOp",EDGE,"E13.top")])],"isStart":false});
            var Q74;
            Q74=makeQuery(id+"F3.opExtrude","CAP_EDGE",EDGE,{"disambiguationData":[OSD([sQuery(id+"F0.wireOp",EDGE,"E18.0.1.3")])],"isStart":false});
            var Q75;
            Q75=makeQuery(id+"F3.opExtrude","CAP_EDGE",EDGE,{"disambiguationData":[OSD([sQuery(id+"F0.wireOp",EDGE,"E18.0.1.4")])],"isStart":false});
            var Q76;
            Q76=makeQuery(id+"F3.opExtrude","CAP_EDGE",EDGE,{"disambiguationData":[OSD([sQuery(id+"F0.wireOp",EDGE,"E13.right")])],"isStart":false});
            var Q77;
            Q77=makeQuery(id+"F3.opExtrude","CAP_EDGE",EDGE,{"disambiguationData":[OSD([sQuery(id+"F0.wireOp",EDGE,"E14.right")])],"isStart":false});
            var Q78;
            Q78=makeQuery(id+"F3.opExtrude","CAP_EDGE",EDGE,{"disambiguationData":[OSD([sQuery(id+"F0.wireOp",EDGE,"E18.1.0.2")])],"isStart":false});
            var Q79;
            Q79=makeQuery(id+"F3.opExtrude","CAP_EDGE",EDGE,{"disambiguationData":[OSD([sQuery(id+"F0.wireOp",EDGE,"E18.1.0.1")])],"isStart":false});
            var Q80;
            Q80=makeQuery(id+"F3.opExtrude","CAP_EDGE",EDGE,{"disambiguationData":[OSD([sQuery(id+"F0.wireOp",EDGE,"E18.1.1.2")])],"isStart":false});
            var Q81;
            Q81=makeQuery(id+"F3.opExtrude","CAP_EDGE",EDGE,{"disambiguationData":[OSD([sQuery(id+"F0.wireOp",EDGE,"E18.1.1.1")])],"isStart":false});
            var Q82;
            Q82=makeQuery(id+"F3.opExtrude","CAP_EDGE",EDGE,{"disambiguationData":[OSD([sQuery(id+"F0.wireOp",EDGE,"E18.1.0.3")])],"isStart":false});
            var Q83;
            Q83=makeQuery(id+"F3.opExtrude","CAP_EDGE",EDGE,{"disambiguationData":[OSD([sQuery(id+"F0.wireOp",EDGE,"E18.1.0.4")])],"isStart":false});
            var Q84;
            Q84=makeQuery(id+"F3.opExtrude","CAP_EDGE",EDGE,{"disambiguationData":[OSD([sQuery(id+"F0.wireOp",EDGE,"E18.1.1.4")])],"isStart":false});
            var Q85;
            Q85=makeQuery(id+"F3.opExtrude","CAP_EDGE",EDGE,{"disambiguationData":[OSD([sQuery(id+"F0.wireOp",EDGE,"E18.1.1.3")])],"isStart":false});
            var Q86;
            Q86=makeQuery(id+"F3.opExtrude","CAP_EDGE",EDGE,{"disambiguationData":[OSD([sQuery(id+"F0.wireOp",EDGE,"E18.1.2.4")])],"isStart":false});
            var Q87;
            Q87=makeQuery(id+"F3.opExtrude","CAP_EDGE",EDGE,{"disambiguationData":[OSD([sQuery(id+"F0.wireOp",EDGE,"E18.1.2.3")])],"isStart":false});
            var Q88;
            Q88=makeQuery(id+"F3.opExtrude","CAP_EDGE",EDGE,{"disambiguationData":[OSD([sQuery(id+"F0.wireOp",EDGE,"E18.2.1.1")])],"isStart":false});
            var Q89;
            Q89=makeQuery(id+"F3.opExtrude","CAP_EDGE",EDGE,{"disambiguationData":[OSD([sQuery(id+"F0.wireOp",EDGE,"E18.2.1.2")])],"isStart":false});
            var Q90;
            Q90=makeQuery(id+"F3.opExtrude","CAP_EDGE",EDGE,{"disambiguationData":[OSD([sQuery(id+"F0.wireOp",EDGE,"E18.2.0.1")])],"isStart":false});
            var Q91;
            Q91=makeQuery(id+"F3.opExtrude","CAP_EDGE",EDGE,{"disambiguationData":[OSD([sQuery(id+"F0.wireOp",EDGE,"E18.2.0.2")])],"isStart":false});
            var Q92;
            Q92=makeQuery(id+"F3.opExtrude","CAP_EDGE",EDGE,{"disambiguationData":[OSD([sQuery(id+"F0.wireOp",EDGE,"E18.2.2.3")])],"isStart":false});
            var Q93;
            Q93=makeQuery(id+"F3.opExtrude","CAP_EDGE",EDGE,{"disambiguationData":[OSD([sQuery(id+"F0.wireOp",EDGE,"E18.2.2.4")])],"isStart":false});
            var Q94;
            Q94=makeQuery(id+"F3.opExtrude","CAP_EDGE",EDGE,{"disambiguationData":[OSD([sQuery(id+"F0.wireOp",EDGE,"E18.2.1.4")])],"isStart":false});
            var Q95;
            Q95=makeQuery(id+"F3.opExtrude","CAP_EDGE",EDGE,{"disambiguationData":[OSD([sQuery(id+"F0.wireOp",EDGE,"E18.2.1.3")])],"isStart":false});
            var Q96;
            Q96=makeQuery(id+"F3.opExtrude","CAP_EDGE",EDGE,{"disambiguationData":[OSD([sQuery(id+"F0.wireOp",EDGE,"E18.2.0.4")])],"isStart":false});
            var Q97;
            Q97=makeQuery(id+"F3.opExtrude","CAP_EDGE",EDGE,{"disambiguationData":[OSD([sQuery(id+"F0.wireOp",EDGE,"E18.2.0.3")])],"isStart":false});
            var Q98;
            Q98=makeQuery(id+"F3.opExtrude","CAP_EDGE",EDGE,{"disambiguationData":[OSD([sQuery(id+"F0.wireOp",EDGE,"E18.3.0.2")])],"isStart":false});
            var Q99;
            Q99=makeQuery(id+"F3.opExtrude","CAP_EDGE",EDGE,{"disambiguationData":[OSD([sQuery(id+"F0.wireOp",EDGE,"E18.3.0.1")])],"isStart":false});
            var Q100;
            Q100=makeQuery(id+"F3.opExtrude","CAP_EDGE",EDGE,{"disambiguationData":[OSD([sQuery(id+"F0.wireOp",EDGE,"E18.3.1.2")])],"isStart":false});
            var Q101;
            Q101=makeQuery(id+"F3.opExtrude","CAP_EDGE",EDGE,{"disambiguationData":[OSD([sQuery(id+"F0.wireOp",EDGE,"E18.3.1.1")])],"isStart":false});
            var Q102;
            Q102=makeQuery(id+"F3.opExtrude","CAP_EDGE",EDGE,{"disambiguationData":[OSD([sQuery(id+"F0.wireOp",EDGE,"E18.3.0.3")])],"isStart":false});
            var Q103;
            Q103=makeQuery(id+"F3.opExtrude","CAP_EDGE",EDGE,{"disambiguationData":[OSD([sQuery(id+"F0.wireOp",EDGE,"E18.3.0.4")])],"isStart":false});
            var Q104;
            Q104=makeQuery(id+"F3.opExtrude","CAP_EDGE",EDGE,{"disambiguationData":[OSD([sQuery(id+"F0.wireOp",EDGE,"E18.3.1.4")])],"isStart":false});
            var Q105;
            Q105=makeQuery(id+"F3.opExtrude","CAP_EDGE",EDGE,{"disambiguationData":[OSD([sQuery(id+"F0.wireOp",EDGE,"E18.3.1.3")])],"isStart":false});
            var Q106;
            Q106=makeQuery(id+"F3.opExtrude","CAP_EDGE",EDGE,{"disambiguationData":[OSD([sQuery(id+"F0.wireOp",EDGE,"E18.3.2.3")])],"isStart":false});
            var Q107;
            Q107=makeQuery(id+"F3.opExtrude","CAP_EDGE",EDGE,{"disambiguationData":[OSD([sQuery(id+"F0.wireOp",EDGE,"E18.3.2.4")])],"isStart":false});
            var Q108;
            Q108=makeQuery(id+"F3.opExtrude","CAP_EDGE",EDGE,{"disambiguationData":[OSD([sQuery(id+"F0.wireOp",EDGE,"E18.4.1.2")])],"isStart":false});
            var Q109;
            Q109=makeQuery(id+"F3.opExtrude","CAP_EDGE",EDGE,{"disambiguationData":[OSD([sQuery(id+"F0.wireOp",EDGE,"E18.4.1.1")])],"isStart":false});
            var Q110;
            Q110=makeQuery(id+"F3.opExtrude","CAP_EDGE",EDGE,{"disambiguationData":[OSD([sQuery(id+"F0.wireOp",EDGE,"E18.4.1.4")])],"isStart":false});
            var Q111;
            Q111=makeQuery(id+"F3.opExtrude","CAP_EDGE",EDGE,{"disambiguationData":[OSD([sQuery(id+"F0.wireOp",EDGE,"E18.4.1.3")])],"isStart":false});
            var Q112;
            Q112=makeQuery(id+"F3.opExtrude","CAP_EDGE",EDGE,{"disambiguationData":[OSD([sQuery(id+"F0.wireOp",EDGE,"E18.5.1.2")])],"isStart":false});
            var Q113;
            Q113=makeQuery(id+"F3.opExtrude","CAP_EDGE",EDGE,{"disambiguationData":[OSD([sQuery(id+"F0.wireOp",EDGE,"E18.5.1.1")])],"isStart":false});
            var Q114;
            Q114=makeQuery(id+"F3.opExtrude","CAP_EDGE",EDGE,{"disambiguationData":[OSD([sQuery(id+"F0.wireOp",EDGE,"E18.5.0.1")])],"isStart":false});
            var Q115;
            Q115=makeQuery(id+"F3.opExtrude","CAP_EDGE",EDGE,{"disambiguationData":[OSD([sQuery(id+"F0.wireOp",EDGE,"E18.5.0.2")])],"isStart":false});
            var Q116;
            Q116=makeQuery(id+"F3.opExtrude","CAP_EDGE",EDGE,{"disambiguationData":[OSD([sQuery(id+"F0.wireOp",EDGE,"E18.4.0.4")])],"isStart":false});
            var Q117;
            Q117=makeQuery(id+"F3.opExtrude","CAP_EDGE",EDGE,{"disambiguationData":[OSD([sQuery(id+"F0.wireOp",EDGE,"E18.4.0.3")])],"isStart":false});
            var Q118;
            Q118=makeQuery(id+"F3.opExtrude","CAP_EDGE",EDGE,{"disambiguationData":[OSD([sQuery(id+"F0.wireOp",EDGE,"E18.4.0.1")])],"isStart":false});
            var Q119;
            Q119=makeQuery(id+"F3.opExtrude","CAP_EDGE",EDGE,{"disambiguationData":[OSD([sQuery(id+"F0.wireOp",EDGE,"E18.4.0.2")])],"isStart":false});
            fillet(context, id + "F4", {"entities" : qUnion([Q0, Q1, Q2, Q3, Q4, Q5, Q6, Q7, Q8, Q9, Q10, Q11, Q12, Q13, Q14, Q15, Q16, Q17, Q18, Q19, Q20, Q21, Q22, Q23, Q24, Q25, Q26, Q27, Q28, Q29, Q30, Q31, Q32, Q33, Q34, Q35, Q36, Q37, Q38, Q39, Q40, Q41, Q42, Q43, Q44, Q45, Q46, Q47, Q48, Q49, Q50, Q51, Q52, Q53, Q54, Q55, Q56, Q57, Q58, Q59, Q60, Q61, Q62, Q63, Q64, Q65, Q66, Q67, Q68, Q69, Q70, Q71, Q72, Q73, Q74, Q75, Q76, Q77, Q78, Q79, Q80, Q81, Q82, Q83, Q84, Q85, Q86, Q87, Q88, Q89, Q90, Q91, Q92, Q93, Q94, Q95, Q96, Q97, Q98, Q99, Q100, Q101, Q102, Q103, Q104, Q105, Q106, Q107, Q108, Q109, Q110, Q111, Q112, Q113, Q114, Q115, Q116, Q117, Q118, Q119]), "radius" : 0.5 * mm, "tangentPropagation" : true, "allowEdgeOverflow" : false});
        }
        {
            var Q0;
            {var subQ0=sQuery(id+"F0.wireOp",EDGE,"E25");Q0=makeQuery(id+"F2.opExtrude","CAP_EDGE",EDGE,{"disambiguationData":[OSD([subQ0]),TDD([makeQuery(id+"F0.imprint","IMPRINT",EDGE,{"disambiguationData":[TD([[makeQuery(id+"F0.imprint","INTERSECT",VERTEX,{"derivedFrom":[subQ0,sQuery(id+"F0.wireOp",EDGE,"E29")]}),-1.0]])],"derivedFrom":subQ0})])],"isStart":false});}
            var Q1;
            {var subQ0=sQuery(id+"F0.wireOp",EDGE,"E24");Q1=makeQuery(id+"F2.opExtrude","CAP_EDGE",EDGE,{"disambiguationData":[OSD([subQ0]),TDD([makeQuery(id+"F0.imprint","IMPRINT",EDGE,{"disambiguationData":[TD([[makeQuery(id+"F0.imprint","INTERSECT",VERTEX,{"derivedFrom":[subQ0,sQuery(id+"F0.wireOp",EDGE,"E29")]}),-1.0]])],"derivedFrom":subQ0})])],"isStart":false});}
            var Q2;
            {var subQ0=sQuery(id+"F0.wireOp",EDGE,"E32.MirrorCS");Q2=makeQuery(id+"F2.opExtrude","CAP_EDGE",EDGE,{"disambiguationData":[OSD([subQ0]),TDD([makeQuery(id+"F0.imprint","IMPRINT",EDGE,{"disambiguationData":[TD([[makeQuery(id+"F0.imprint","INTERSECT",VERTEX,{"derivedFrom":[sQuery(id+"F0.wireOp",EDGE,"E22"),subQ0]}),1.0]])],"derivedFrom":subQ0})])],"isStart":false});}
            var Q3;
            {var subQ0=sQuery(id+"F0.wireOp",EDGE,"E31.0");Q3=makeQuery(id+"F2.opExtrude","CAP_EDGE",EDGE,{"disambiguationData":[OSD([subQ0]),TDD([makeQuery(id+"F0.imprint","IMPRINT",EDGE,{"disambiguationData":[TD([[makeQuery(id+"F0.imprint","INTERSECT",VERTEX,{"derivedFrom":[sQuery(id+"F0.wireOp",EDGE,"E25"),subQ0]}),1.0]])],"derivedFrom":subQ0})])],"isStart":false});}
            var Q4;
            {var subQ0=sQuery(id+"F0.wireOp",EDGE,"E32.MirrorCS");Q4=makeQuery(id+"F2.opExtrude","CAP_EDGE",EDGE,{"disambiguationData":[OSD([subQ0]),TDD([makeQuery(id+"F0.imprint","IMPRINT",EDGE,{"disambiguationData":[TD([[makeQuery(id+"F0.imprint","INTERSECT",VERTEX,{"derivedFrom":[sQuery(id+"F0.wireOp",EDGE,"E25"),subQ0]}),1.0]])],"derivedFrom":subQ0})])],"isStart":false});}
            var Q5;
            {var subQ0=sQuery(id+"F0.wireOp",EDGE,"E26");Q5=makeQuery(id+"F2.opExtrude","CAP_EDGE",EDGE,{"disambiguationData":[OSD([subQ0]),TDD([makeQuery(id+"F0.imprint","IMPRINT",EDGE,{"disambiguationData":[TD([[makeQuery(id+"F0.imprint","INTERSECT",VERTEX,{"derivedFrom":[subQ0,sQuery(id+"F0.wireOp",EDGE,"E29")]}),-1.0]])],"derivedFrom":subQ0})])],"isStart":false});}
            var Q6;
            {var subQ0=sQuery(id+"F0.wireOp",EDGE,"E27");Q6=makeQuery(id+"F2.opExtrude","CAP_EDGE",EDGE,{"disambiguationData":[OSD([subQ0]),TDD([makeQuery(id+"F0.imprint","IMPRINT",EDGE,{"disambiguationData":[TD([[makeQuery(id+"F0.imprint","INTERSECT",VERTEX,{"derivedFrom":[subQ0,sQuery(id+"F0.wireOp",EDGE,"E31.0")]}),-1.0]])],"derivedFrom":subQ0})])],"isStart":false});}
            var Q7;
            {var subQ0=sQuery(id+"F0.wireOp",EDGE,"E32.MirrorCS");Q7=makeQuery(id+"F2.opExtrude","CAP_EDGE",EDGE,{"disambiguationData":[OSD([subQ0]),TDD([makeQuery(id+"F0.imprint","IMPRINT",EDGE,{"disambiguationData":[TD([[makeQuery(id+"F0.imprint","INTERSECT",VERTEX,{"derivedFrom":[sQuery(id+"F0.wireOp",EDGE,"E29"),subQ0]}),-1.0]])],"derivedFrom":subQ0})])],"isStart":false});}
            var Q8;
            {var subQ0=sQuery(id+"F0.wireOp",EDGE,"E31.0");Q8=makeQuery(id+"F2.opExtrude","CAP_EDGE",EDGE,{"disambiguationData":[OSD([subQ0]),TDD([makeQuery(id+"F0.imprint","IMPRINT",EDGE,{"disambiguationData":[TD([[makeQuery(id+"F0.imprint","INTERSECT",VERTEX,{"derivedFrom":[subQ0,sQuery(id+"F0.wireOp",EDGE,"E34.MirrorCS")]}),-1.0]])],"derivedFrom":subQ0})])],"isStart":false});}
            var Q9;
            {var subQ0=sQuery(id+"F0.wireOp",EDGE,"E26");Q9=makeQuery(id+"F2.opExtrude","CAP_EDGE",EDGE,{"disambiguationData":[OSD([subQ0]),TDD([makeQuery(id+"F0.imprint","IMPRINT",EDGE,{"disambiguationData":[TD([[makeQuery(id+"F0.imprint","INTERSECT",VERTEX,{"derivedFrom":[subQ0,sQuery(id+"F0.wireOp",EDGE,"E31.0")]}),-1.0]])],"derivedFrom":subQ0})])],"isStart":false});}
            var Q10;
            {var subQ0=sQuery(id+"F0.wireOp",EDGE,"E34.MirrorCS");Q10=makeQuery(id+"F2.opExtrude","CAP_EDGE",EDGE,{"disambiguationData":[OSD([subQ0]),TDD([makeQuery(id+"F0.imprint","IMPRINT",EDGE,{"disambiguationData":[TD([[makeQuery(id+"F0.imprint","INTERSECT",VERTEX,{"derivedFrom":[sQuery(id+"F0.wireOp",EDGE,"E31.0"),subQ0]}),-1.0]])],"derivedFrom":subQ0})])],"isStart":false});}
            var Q11;
            {var subQ0=sQuery(id+"F0.wireOp",EDGE,"E33.0");Q11=makeQuery(id+"F2.opExtrude","CAP_EDGE",EDGE,{"disambiguationData":[OSD([subQ0]),TDD([makeQuery(id+"F0.imprint","IMPRINT",EDGE,{"disambiguationData":[TD([[makeQuery(id+"F0.imprint","INTERSECT",VERTEX,{"derivedFrom":[subQ0,sQuery(id+"F0.wireOp",EDGE,"E36.MirrorCS")]}),-1.0]])],"derivedFrom":subQ0})])],"isStart":false});}
            var Q12;
            {var subQ0=sQuery(id+"F0.wireOp",EDGE,"E36.MirrorCS");Q12=makeQuery(id+"F2.opExtrude","CAP_EDGE",EDGE,{"disambiguationData":[OSD([subQ0]),TDD([makeQuery(id+"F0.imprint","IMPRINT",EDGE,{"disambiguationData":[TD([[makeQuery(id+"F0.imprint","INTERSECT",VERTEX,{"derivedFrom":[sQuery(id+"F0.wireOp",EDGE,"E33.0"),subQ0]}),-1.0]])],"derivedFrom":subQ0})])],"isStart":false});}
            var Q13;
            {var subQ0=sQuery(id+"F0.wireOp",EDGE,"E35.0");Q13=makeQuery(id+"F2.opExtrude","CAP_EDGE",EDGE,{"disambiguationData":[OSD([subQ0]),TDD([makeQuery(id+"F0.imprint","IMPRINT",EDGE,{"disambiguationData":[TD([[makeQuery(id+"F0.imprint","INTERSECT",VERTEX,{"derivedFrom":[subQ0,sQuery(id+"F0.wireOp",EDGE,"E38.0")]}),-1.0]])],"derivedFrom":subQ0})])],"isStart":false});}
            var Q14;
            {var subQ0=sQuery(id+"F0.wireOp",EDGE,"E38.0");Q14=makeQuery(id+"F2.opExtrude","CAP_EDGE",EDGE,{"disambiguationData":[OSD([subQ0]),TDD([makeQuery(id+"F0.imprint","IMPRINT",EDGE,{"disambiguationData":[TD([[makeQuery(id+"F0.imprint","INTERSECT",VERTEX,{"derivedFrom":[sQuery(id+"F0.wireOp",EDGE,"E35.0"),subQ0]}),-1.0]])],"derivedFrom":subQ0})])],"isStart":false});}
            var Q15;
            {var subQ0=sQuery(id+"F0.wireOp",EDGE,"E37.0");Q15=makeQuery(id+"F2.opExtrude","CAP_EDGE",EDGE,{"disambiguationData":[OSD([subQ0]),TDD([makeQuery(id+"F0.imprint","IMPRINT",EDGE,{"disambiguationData":[TD([[makeQuery(id+"F0.imprint","INTERSECT",VERTEX,{"derivedFrom":[subQ0,sQuery(id+"F0.wireOp",EDGE,"E40.0")]}),-1.0]])],"derivedFrom":subQ0})])],"isStart":false});}
            var Q16;
            {var subQ0=sQuery(id+"F0.wireOp",EDGE,"E40.0");Q16=makeQuery(id+"F2.opExtrude","CAP_EDGE",EDGE,{"disambiguationData":[OSD([subQ0]),TDD([makeQuery(id+"F0.imprint","IMPRINT",EDGE,{"disambiguationData":[TD([[makeQuery(id+"F0.imprint","INTERSECT",VERTEX,{"derivedFrom":[sQuery(id+"F0.wireOp",EDGE,"E37.0"),subQ0]}),-1.0]])],"derivedFrom":subQ0})])],"isStart":false});}
            var Q17;
            {var subQ0=sQuery(id+"F0.wireOp",EDGE,"E39.0");Q17=makeQuery(id+"F2.opExtrude","CAP_EDGE",EDGE,{"disambiguationData":[OSD([subQ0]),TDD([makeQuery(id+"F0.imprint","IMPRINT",EDGE,{"disambiguationData":[TD([[makeQuery(id+"F0.imprint","INTERSECT",VERTEX,{"derivedFrom":[subQ0,sQuery(id+"F0.wireOp",EDGE,"E44.0")]}),-1.0]])],"derivedFrom":subQ0})])],"isStart":false});}
            var Q18;
            {var subQ0=sQuery(id+"F0.wireOp",EDGE,"E44.0");Q18=makeQuery(id+"F2.opExtrude","CAP_EDGE",EDGE,{"disambiguationData":[OSD([subQ0]),TDD([makeQuery(id+"F0.imprint","IMPRINT",EDGE,{"disambiguationData":[TD([[makeQuery(id+"F0.imprint","INTERSECT",VERTEX,{"derivedFrom":[sQuery(id+"F0.wireOp",EDGE,"E39.0"),subQ0]}),-1.0]])],"derivedFrom":subQ0})])],"isStart":false});}
            var Q19;
            {var subQ0=sQuery(id+"F0.wireOp",EDGE,"E43.0");Q19=makeQuery(id+"F2.opExtrude","CAP_EDGE",EDGE,{"disambiguationData":[OSD([subQ0]),TDD([makeQuery(id+"F0.imprint","IMPRINT",EDGE,{"disambiguationData":[TD([[makeQuery(id+"F0.imprint","INTERSECT",VERTEX,{"derivedFrom":[sQuery(id+"F0.wireOp",EDGE,"E42.0"),subQ0]}),-1.0]])],"derivedFrom":subQ0})])],"isStart":false});}
            var Q20;
            {var subQ0=sQuery(id+"F0.wireOp",EDGE,"E42.0");Q20=makeQuery(id+"F2.opExtrude","CAP_EDGE",EDGE,{"disambiguationData":[OSD([subQ0]),TDD([makeQuery(id+"F0.imprint","IMPRINT",EDGE,{"disambiguationData":[TD([[makeQuery(id+"F0.imprint","INTERSECT",VERTEX,{"derivedFrom":[subQ0,sQuery(id+"F0.wireOp",EDGE,"E43.0")]}),-1.0]])],"derivedFrom":subQ0})])],"isStart":false});}
            var Q21;
            {var subQ0=sQuery(id+"F0.wireOp",EDGE,"E41.0");Q21=makeQuery(id+"F2.opExtrude","CAP_EDGE",EDGE,{"disambiguationData":[OSD([subQ0]),TDD([makeQuery(id+"F0.imprint","IMPRINT",EDGE,{"disambiguationData":[TD([[makeQuery(id+"F0.imprint","INTERSECT",VERTEX,{"derivedFrom":[sQuery(id+"F0.wireOp",EDGE,"E30.8.0"),subQ0]}),-1.0]])],"derivedFrom":subQ0})])],"isStart":false});}
            var Q22;
            {var subQ0=sQuery(id+"F0.wireOp",EDGE,"E27");Q22=makeQuery(id+"F2.opExtrude","CAP_EDGE",EDGE,{"disambiguationData":[OSD([subQ0]),TDD([makeQuery(id+"F0.imprint","IMPRINT",EDGE,{"disambiguationData":[TD([[makeQuery(id+"F0.imprint","INTERSECT",VERTEX,{"derivedFrom":[subQ0,sQuery(id+"F0.wireOp",EDGE,"E30.8.0")]}),1.0]])],"derivedFrom":subQ0})])],"isStart":false});}
            var Q23;
            {var subQ0=sQuery(id+"F0.wireOp",EDGE,"E26");Q23=makeQuery(id+"F2.opExtrude","CAP_EDGE",EDGE,{"disambiguationData":[OSD([subQ0]),TDD([makeQuery(id+"F0.imprint","IMPRINT",EDGE,{"disambiguationData":[TD([[makeQuery(id+"F0.imprint","INTERSECT",VERTEX,{"derivedFrom":[subQ0,sQuery(id+"F0.wireOp",EDGE,"E43.0")]}),-1.0]])],"derivedFrom":subQ0})])],"isStart":false});}
            var Q24;
            {var subQ0=sQuery(id+"F0.wireOp",EDGE,"E27");Q24=makeQuery(id+"F2.opExtrude","CAP_EDGE",EDGE,{"disambiguationData":[OSD([subQ0]),TDD([makeQuery(id+"F0.imprint","IMPRINT",EDGE,{"disambiguationData":[TD([[makeQuery(id+"F0.imprint","INTERSECT",VERTEX,{"derivedFrom":[subQ0,sQuery(id+"F0.wireOp",EDGE,"E43.0")]}),-1.0]])],"derivedFrom":subQ0})])],"isStart":false});}
            var Q25;
            {var subQ0=sQuery(id+"F0.wireOp",EDGE,"E27");Q25=makeQuery(id+"F2.opExtrude","CAP_EDGE",EDGE,{"disambiguationData":[OSD([subQ0]),TDD([makeQuery(id+"F0.imprint","IMPRINT",EDGE,{"disambiguationData":[TD([[makeQuery(id+"F0.imprint","INTERSECT",VERTEX,{"derivedFrom":[subQ0,sQuery(id+"F0.wireOp",EDGE,"E39.0")]}),-1.0]])],"derivedFrom":subQ0})])],"isStart":false});}
            var Q26;
            {var subQ0=sQuery(id+"F0.wireOp",EDGE,"E26");Q26=makeQuery(id+"F2.opExtrude","CAP_EDGE",EDGE,{"disambiguationData":[OSD([subQ0]),TDD([makeQuery(id+"F0.imprint","IMPRINT",EDGE,{"disambiguationData":[TD([[makeQuery(id+"F0.imprint","INTERSECT",VERTEX,{"derivedFrom":[subQ0,sQuery(id+"F0.wireOp",EDGE,"E39.0")]}),-1.0]])],"derivedFrom":subQ0})])],"isStart":false});}
            var Q27;
            {var subQ0=sQuery(id+"F0.wireOp",EDGE,"E26");Q27=makeQuery(id+"F2.opExtrude","CAP_EDGE",EDGE,{"disambiguationData":[OSD([subQ0]),TDD([makeQuery(id+"F0.imprint","IMPRINT",EDGE,{"disambiguationData":[TD([[makeQuery(id+"F0.imprint","INTERSECT",VERTEX,{"derivedFrom":[subQ0,sQuery(id+"F0.wireOp",EDGE,"E37.0")]}),-1.0]])],"derivedFrom":subQ0})])],"isStart":false});}
            var Q28;
            {var subQ0=sQuery(id+"F0.wireOp",EDGE,"E27");Q28=makeQuery(id+"F2.opExtrude","CAP_EDGE",EDGE,{"disambiguationData":[OSD([subQ0]),TDD([makeQuery(id+"F0.imprint","IMPRINT",EDGE,{"disambiguationData":[TD([[makeQuery(id+"F0.imprint","INTERSECT",VERTEX,{"derivedFrom":[subQ0,sQuery(id+"F0.wireOp",EDGE,"E37.0")]}),-1.0]])],"derivedFrom":subQ0})])],"isStart":false});}
            var Q29;
            {var subQ0=sQuery(id+"F0.wireOp",EDGE,"E26");Q29=makeQuery(id+"F2.opExtrude","CAP_EDGE",EDGE,{"disambiguationData":[OSD([subQ0]),TDD([makeQuery(id+"F0.imprint","IMPRINT",EDGE,{"disambiguationData":[TD([[makeQuery(id+"F0.imprint","INTERSECT",VERTEX,{"derivedFrom":[subQ0,sQuery(id+"F0.wireOp",EDGE,"E35.0")]}),-1.0]])],"derivedFrom":subQ0})])],"isStart":false});}
            var Q30;
            {var subQ0=sQuery(id+"F0.wireOp",EDGE,"E27");Q30=makeQuery(id+"F2.opExtrude","CAP_EDGE",EDGE,{"disambiguationData":[OSD([subQ0]),TDD([makeQuery(id+"F0.imprint","IMPRINT",EDGE,{"disambiguationData":[TD([[makeQuery(id+"F0.imprint","INTERSECT",VERTEX,{"derivedFrom":[subQ0,sQuery(id+"F0.wireOp",EDGE,"E35.0")]}),-1.0]])],"derivedFrom":subQ0})])],"isStart":false});}
            var Q31;
            {var subQ0=sQuery(id+"F0.wireOp",EDGE,"E27");Q31=makeQuery(id+"F2.opExtrude","CAP_EDGE",EDGE,{"disambiguationData":[OSD([subQ0]),TDD([makeQuery(id+"F0.imprint","IMPRINT",EDGE,{"disambiguationData":[TD([[makeQuery(id+"F0.imprint","INTERSECT",VERTEX,{"derivedFrom":[subQ0,sQuery(id+"F0.wireOp",EDGE,"E33.0")]}),-1.0]])],"derivedFrom":subQ0})])],"isStart":false});}
            var Q32;
            {var subQ0=sQuery(id+"F0.wireOp",EDGE,"E26");Q32=makeQuery(id+"F2.opExtrude","CAP_EDGE",EDGE,{"disambiguationData":[OSD([subQ0]),TDD([makeQuery(id+"F0.imprint","IMPRINT",EDGE,{"disambiguationData":[TD([[makeQuery(id+"F0.imprint","INTERSECT",VERTEX,{"derivedFrom":[subQ0,sQuery(id+"F0.wireOp",EDGE,"E33.0")]}),-1.0]])],"derivedFrom":subQ0})])],"isStart":false});}
            var Q33;
            {var subQ0=sQuery(id+"F0.wireOp",EDGE,"E26");Q33=makeQuery(id+"F2.opExtrude","CAP_EDGE",EDGE,{"disambiguationData":[OSD([subQ0]),TDD([makeQuery(id+"F0.imprint","IMPRINT",EDGE,{"disambiguationData":[TD([[makeQuery(id+"F0.imprint","INTERSECT",VERTEX,{"derivedFrom":[subQ0,sQuery(id+"F0.wireOp",EDGE,"E30.8.0")]}),1.0]])],"derivedFrom":subQ0})])],"isStart":false});}
            var Q34;
            {var subQ0=sQuery(id+"F0.wireOp",EDGE,"E41.0");Q34=makeQuery(id+"F2.opExtrude","CAP_EDGE",EDGE,{"disambiguationData":[OSD([subQ0]),TDD([makeQuery(id+"F0.imprint","IMPRINT",EDGE,{"disambiguationData":[TD([[makeQuery(id+"F0.imprint","INTERSECT",VERTEX,{"derivedFrom":[sQuery(id+"F0.wireOp",EDGE,"E25"),subQ0]}),1.0]])],"derivedFrom":subQ0})])],"isStart":false});}
            var Q35;
            {var subQ0=sQuery(id+"F0.wireOp",EDGE,"E42.0");Q35=makeQuery(id+"F2.opExtrude","CAP_EDGE",EDGE,{"disambiguationData":[OSD([subQ0]),TDD([makeQuery(id+"F0.imprint","IMPRINT",EDGE,{"disambiguationData":[TD([[makeQuery(id+"F0.imprint","INTERSECT",VERTEX,{"derivedFrom":[sQuery(id+"F0.wireOp",EDGE,"E25"),subQ0]}),1.0]])],"derivedFrom":subQ0})])],"isStart":false});}
            var Q36;
            {var subQ0=sQuery(id+"F0.wireOp",EDGE,"E43.0");Q36=makeQuery(id+"F2.opExtrude","CAP_EDGE",EDGE,{"disambiguationData":[OSD([subQ0]),TDD([makeQuery(id+"F0.imprint","IMPRINT",EDGE,{"disambiguationData":[TD([[makeQuery(id+"F0.imprint","INTERSECT",VERTEX,{"derivedFrom":[sQuery(id+"F0.wireOp",EDGE,"E25"),subQ0]}),1.0]])],"derivedFrom":subQ0})])],"isStart":false});}
            var Q37;
            {var subQ0=sQuery(id+"F0.wireOp",EDGE,"E44.0");Q37=makeQuery(id+"F2.opExtrude","CAP_EDGE",EDGE,{"disambiguationData":[OSD([subQ0]),TDD([makeQuery(id+"F0.imprint","IMPRINT",EDGE,{"disambiguationData":[TD([[makeQuery(id+"F0.imprint","INTERSECT",VERTEX,{"derivedFrom":[sQuery(id+"F0.wireOp",EDGE,"E25"),subQ0]}),1.0]])],"derivedFrom":subQ0})])],"isStart":false});}
            var Q38;
            {var subQ0=sQuery(id+"F0.wireOp",EDGE,"E39.0");Q38=makeQuery(id+"F2.opExtrude","CAP_EDGE",EDGE,{"disambiguationData":[OSD([subQ0]),TDD([makeQuery(id+"F0.imprint","IMPRINT",EDGE,{"disambiguationData":[TD([[makeQuery(id+"F0.imprint","INTERSECT",VERTEX,{"derivedFrom":[sQuery(id+"F0.wireOp",EDGE,"E25"),subQ0]}),1.0]])],"derivedFrom":subQ0})])],"isStart":false});}
            var Q39;
            {var subQ0=sQuery(id+"F0.wireOp",EDGE,"E40.0");Q39=makeQuery(id+"F2.opExtrude","CAP_EDGE",EDGE,{"disambiguationData":[OSD([subQ0]),TDD([makeQuery(id+"F0.imprint","IMPRINT",EDGE,{"disambiguationData":[TD([[makeQuery(id+"F0.imprint","INTERSECT",VERTEX,{"derivedFrom":[sQuery(id+"F0.wireOp",EDGE,"E25"),subQ0]}),1.0]])],"derivedFrom":subQ0})])],"isStart":false});}
            var Q40;
            {var subQ0=sQuery(id+"F0.wireOp",EDGE,"E38.0");Q40=makeQuery(id+"F2.opExtrude","CAP_EDGE",EDGE,{"disambiguationData":[OSD([subQ0]),TDD([makeQuery(id+"F0.imprint","IMPRINT",EDGE,{"disambiguationData":[TD([[makeQuery(id+"F0.imprint","INTERSECT",VERTEX,{"derivedFrom":[sQuery(id+"F0.wireOp",EDGE,"E25"),subQ0]}),1.0]])],"derivedFrom":subQ0})])],"isStart":false});}
            var Q41;
            {var subQ0=sQuery(id+"F0.wireOp",EDGE,"E35.0");Q41=makeQuery(id+"F2.opExtrude","CAP_EDGE",EDGE,{"disambiguationData":[OSD([subQ0]),TDD([makeQuery(id+"F0.imprint","IMPRINT",EDGE,{"disambiguationData":[TD([[makeQuery(id+"F0.imprint","INTERSECT",VERTEX,{"derivedFrom":[sQuery(id+"F0.wireOp",EDGE,"E25"),subQ0]}),1.0]])],"derivedFrom":subQ0})])],"isStart":false});}
            var Q42;
            {var subQ0=sQuery(id+"F0.wireOp",EDGE,"E36.MirrorCS");Q42=makeQuery(id+"F2.opExtrude","CAP_EDGE",EDGE,{"disambiguationData":[OSD([subQ0]),TDD([makeQuery(id+"F0.imprint","IMPRINT",EDGE,{"disambiguationData":[TD([[makeQuery(id+"F0.imprint","INTERSECT",VERTEX,{"derivedFrom":[sQuery(id+"F0.wireOp",EDGE,"E25"),subQ0]}),1.0]])],"derivedFrom":subQ0})])],"isStart":false});}
            var Q43;
            {var subQ0=sQuery(id+"F0.wireOp",EDGE,"E33.0");Q43=makeQuery(id+"F2.opExtrude","CAP_EDGE",EDGE,{"disambiguationData":[OSD([subQ0]),TDD([makeQuery(id+"F0.imprint","IMPRINT",EDGE,{"disambiguationData":[TD([[makeQuery(id+"F0.imprint","INTERSECT",VERTEX,{"derivedFrom":[sQuery(id+"F0.wireOp",EDGE,"E25"),subQ0]}),1.0]])],"derivedFrom":subQ0})])],"isStart":false});}
            var Q44;
            {var subQ0=sQuery(id+"F0.wireOp",EDGE,"E34.MirrorCS");Q44=makeQuery(id+"F2.opExtrude","CAP_EDGE",EDGE,{"disambiguationData":[OSD([subQ0]),TDD([makeQuery(id+"F0.imprint","IMPRINT",EDGE,{"disambiguationData":[TD([[makeQuery(id+"F0.imprint","INTERSECT",VERTEX,{"derivedFrom":[sQuery(id+"F0.wireOp",EDGE,"E25"),subQ0]}),1.0]])],"derivedFrom":subQ0})])],"isStart":false});}
            var Q45;
            {var subQ0=sQuery(id+"F0.wireOp",EDGE,"E25");Q45=makeQuery(id+"F2.opExtrude","CAP_EDGE",EDGE,{"disambiguationData":[OSD([subQ0]),TDD([makeQuery(id+"F0.imprint","IMPRINT",EDGE,{"disambiguationData":[TD([[makeQuery(id+"F0.imprint","INTERSECT",VERTEX,{"derivedFrom":[subQ0,sQuery(id+"F0.wireOp",EDGE,"E31.0")]}),-1.0]])],"derivedFrom":subQ0})])],"isStart":false});}
            var Q46;
            {var subQ0=sQuery(id+"F0.wireOp",EDGE,"E24");Q46=makeQuery(id+"F2.opExtrude","CAP_EDGE",EDGE,{"disambiguationData":[OSD([subQ0]),TDD([makeQuery(id+"F0.imprint","IMPRINT",EDGE,{"disambiguationData":[TD([[makeQuery(id+"F0.imprint","INTERSECT",VERTEX,{"derivedFrom":[subQ0,sQuery(id+"F0.wireOp",EDGE,"E31.0")]}),-1.0]])],"derivedFrom":subQ0})])],"isStart":false});}
            var Q47;
            {var subQ0=sQuery(id+"F0.wireOp",EDGE,"E25");Q47=makeQuery(id+"F2.opExtrude","CAP_EDGE",EDGE,{"disambiguationData":[OSD([subQ0]),TDD([makeQuery(id+"F0.imprint","IMPRINT",EDGE,{"disambiguationData":[TD([[makeQuery(id+"F0.imprint","INTERSECT",VERTEX,{"derivedFrom":[subQ0,sQuery(id+"F0.wireOp",EDGE,"E33.0")]}),-1.0]])],"derivedFrom":subQ0})])],"isStart":false});}
            var Q48;
            {var subQ0=sQuery(id+"F0.wireOp",EDGE,"E24");Q48=makeQuery(id+"F2.opExtrude","CAP_EDGE",EDGE,{"disambiguationData":[OSD([subQ0]),TDD([makeQuery(id+"F0.imprint","IMPRINT",EDGE,{"disambiguationData":[TD([[makeQuery(id+"F0.imprint","INTERSECT",VERTEX,{"derivedFrom":[subQ0,sQuery(id+"F0.wireOp",EDGE,"E33.0")]}),-1.0]])],"derivedFrom":subQ0})])],"isStart":false});}
            var Q49;
            {var subQ0=sQuery(id+"F0.wireOp",EDGE,"E25");Q49=makeQuery(id+"F2.opExtrude","CAP_EDGE",EDGE,{"disambiguationData":[OSD([subQ0]),TDD([makeQuery(id+"F0.imprint","IMPRINT",EDGE,{"disambiguationData":[TD([[makeQuery(id+"F0.imprint","INTERSECT",VERTEX,{"derivedFrom":[subQ0,sQuery(id+"F0.wireOp",EDGE,"E35.0")]}),-1.0]])],"derivedFrom":subQ0})])],"isStart":false});}
            var Q50;
            {var subQ0=sQuery(id+"F0.wireOp",EDGE,"E24");Q50=makeQuery(id+"F2.opExtrude","CAP_EDGE",EDGE,{"disambiguationData":[OSD([subQ0]),TDD([makeQuery(id+"F0.imprint","IMPRINT",EDGE,{"disambiguationData":[TD([[makeQuery(id+"F0.imprint","INTERSECT",VERTEX,{"derivedFrom":[subQ0,sQuery(id+"F0.wireOp",EDGE,"E35.0")]}),-1.0]])],"derivedFrom":subQ0})])],"isStart":false});}
            var Q51;
            {var subQ0=sQuery(id+"F0.wireOp",EDGE,"E25");Q51=makeQuery(id+"F2.opExtrude","CAP_EDGE",EDGE,{"disambiguationData":[OSD([subQ0]),TDD([makeQuery(id+"F0.imprint","IMPRINT",EDGE,{"disambiguationData":[TD([[makeQuery(id+"F0.imprint","INTERSECT",VERTEX,{"derivedFrom":[subQ0,sQuery(id+"F0.wireOp",EDGE,"E37.0")]}),-1.0]])],"derivedFrom":subQ0})])],"isStart":false});}
            var Q52;
            {var subQ0=sQuery(id+"F0.wireOp",EDGE,"E24");Q52=makeQuery(id+"F2.opExtrude","CAP_EDGE",EDGE,{"disambiguationData":[OSD([subQ0]),TDD([makeQuery(id+"F0.imprint","IMPRINT",EDGE,{"disambiguationData":[TD([[makeQuery(id+"F0.imprint","INTERSECT",VERTEX,{"derivedFrom":[subQ0,sQuery(id+"F0.wireOp",EDGE,"E37.0")]}),-1.0]])],"derivedFrom":subQ0})])],"isStart":false});}
            var Q53;
            {var subQ0=sQuery(id+"F0.wireOp",EDGE,"E25");Q53=makeQuery(id+"F2.opExtrude","CAP_EDGE",EDGE,{"disambiguationData":[OSD([subQ0]),TDD([makeQuery(id+"F0.imprint","IMPRINT",EDGE,{"disambiguationData":[TD([[makeQuery(id+"F0.imprint","INTERSECT",VERTEX,{"derivedFrom":[subQ0,sQuery(id+"F0.wireOp",EDGE,"E39.0")]}),-1.0]])],"derivedFrom":subQ0})])],"isStart":false});}
            var Q54;
            {var subQ0=sQuery(id+"F0.wireOp",EDGE,"E24");Q54=makeQuery(id+"F2.opExtrude","CAP_EDGE",EDGE,{"disambiguationData":[OSD([subQ0]),TDD([makeQuery(id+"F0.imprint","IMPRINT",EDGE,{"disambiguationData":[TD([[makeQuery(id+"F0.imprint","INTERSECT",VERTEX,{"derivedFrom":[subQ0,sQuery(id+"F0.wireOp",EDGE,"E39.0")]}),-1.0]])],"derivedFrom":subQ0})])],"isStart":false});}
            var Q55;
            {var subQ0=sQuery(id+"F0.wireOp",EDGE,"E25");Q55=makeQuery(id+"F2.opExtrude","CAP_EDGE",EDGE,{"disambiguationData":[OSD([subQ0]),TDD([makeQuery(id+"F0.imprint","IMPRINT",EDGE,{"disambiguationData":[TD([[makeQuery(id+"F0.imprint","INTERSECT",VERTEX,{"derivedFrom":[subQ0,sQuery(id+"F0.wireOp",EDGE,"E43.0")]}),-1.0]])],"derivedFrom":subQ0})])],"isStart":false});}
            var Q56;
            {var subQ0=sQuery(id+"F0.wireOp",EDGE,"E24");Q56=makeQuery(id+"F2.opExtrude","CAP_EDGE",EDGE,{"disambiguationData":[OSD([subQ0]),TDD([makeQuery(id+"F0.imprint","IMPRINT",EDGE,{"disambiguationData":[TD([[makeQuery(id+"F0.imprint","INTERSECT",VERTEX,{"derivedFrom":[subQ0,sQuery(id+"F0.wireOp",EDGE,"E43.0")]}),-1.0]])],"derivedFrom":subQ0})])],"isStart":false});}
            var Q57;
            {var subQ0=sQuery(id+"F0.wireOp",EDGE,"E24");Q57=makeQuery(id+"F2.opExtrude","CAP_EDGE",EDGE,{"disambiguationData":[OSD([subQ0]),TDD([makeQuery(id+"F0.imprint","IMPRINT",EDGE,{"disambiguationData":[TD([[makeQuery(id+"F0.imprint","INTERSECT",VERTEX,{"derivedFrom":[subQ0,sQuery(id+"F0.wireOp",EDGE,"E30.8.0")]}),1.0]])],"derivedFrom":subQ0})])],"isStart":false});}
            var Q58;
            {var subQ0=sQuery(id+"F0.wireOp",EDGE,"E41.0");Q58=makeQuery(id+"F2.opExtrude","CAP_EDGE",EDGE,{"disambiguationData":[OSD([subQ0]),TDD([makeQuery(id+"F0.imprint","IMPRINT",EDGE,{"disambiguationData":[TD([[makeQuery(id+"F0.imprint","INTERSECT",VERTEX,{"derivedFrom":[sQuery(id+"F0.wireOp",EDGE,"E22"),subQ0]}),1.0]])],"derivedFrom":subQ0})])],"isStart":false});}
            var Q59;
            {var subQ0=sQuery(id+"F0.wireOp",EDGE,"E42.0");Q59=makeQuery(id+"F2.opExtrude","CAP_EDGE",EDGE,{"disambiguationData":[OSD([subQ0]),TDD([makeQuery(id+"F0.imprint","IMPRINT",EDGE,{"disambiguationData":[TD([[makeQuery(id+"F0.imprint","INTERSECT",VERTEX,{"derivedFrom":[sQuery(id+"F0.wireOp",EDGE,"E22"),subQ0]}),1.0]])],"derivedFrom":subQ0})])],"isStart":false});}
            var Q60;
            {var subQ0=sQuery(id+"F0.wireOp",EDGE,"E25");Q60=makeQuery(id+"F2.opExtrude","CAP_EDGE",EDGE,{"disambiguationData":[OSD([subQ0]),TDD([makeQuery(id+"F0.imprint","IMPRINT",EDGE,{"disambiguationData":[TD([[makeQuery(id+"F0.imprint","INTERSECT",VERTEX,{"derivedFrom":[subQ0,sQuery(id+"F0.wireOp",EDGE,"E30.8.0")]}),1.0]])],"derivedFrom":subQ0})])],"isStart":false});}
            var Q61;
            {var subQ0=sQuery(id+"F0.wireOp",EDGE,"E43.0");Q61=makeQuery(id+"F2.opExtrude","CAP_EDGE",EDGE,{"disambiguationData":[OSD([subQ0]),TDD([makeQuery(id+"F0.imprint","IMPRINT",EDGE,{"disambiguationData":[TD([[makeQuery(id+"F0.imprint","INTERSECT",VERTEX,{"derivedFrom":[sQuery(id+"F0.wireOp",EDGE,"E22"),subQ0]}),1.0]])],"derivedFrom":subQ0})])],"isStart":false});}
            var Q62;
            {var subQ0=sQuery(id+"F0.wireOp",EDGE,"E44.0");Q62=makeQuery(id+"F2.opExtrude","CAP_EDGE",EDGE,{"disambiguationData":[OSD([subQ0]),TDD([makeQuery(id+"F0.imprint","IMPRINT",EDGE,{"disambiguationData":[TD([[makeQuery(id+"F0.imprint","INTERSECT",VERTEX,{"derivedFrom":[sQuery(id+"F0.wireOp",EDGE,"E22"),subQ0]}),1.0]])],"derivedFrom":subQ0})])],"isStart":false});}
            var Q63;
            {var subQ0=sQuery(id+"F0.wireOp",EDGE,"E39.0");Q63=makeQuery(id+"F2.opExtrude","CAP_EDGE",EDGE,{"disambiguationData":[OSD([subQ0]),TDD([makeQuery(id+"F0.imprint","IMPRINT",EDGE,{"disambiguationData":[TD([[makeQuery(id+"F0.imprint","INTERSECT",VERTEX,{"derivedFrom":[sQuery(id+"F0.wireOp",EDGE,"E22"),subQ0]}),1.0]])],"derivedFrom":subQ0})])],"isStart":false});}
            var Q64;
            {var subQ0=sQuery(id+"F0.wireOp",EDGE,"E40.0");Q64=makeQuery(id+"F2.opExtrude","CAP_EDGE",EDGE,{"disambiguationData":[OSD([subQ0]),TDD([makeQuery(id+"F0.imprint","IMPRINT",EDGE,{"disambiguationData":[TD([[makeQuery(id+"F0.imprint","INTERSECT",VERTEX,{"derivedFrom":[sQuery(id+"F0.wireOp",EDGE,"E22"),subQ0]}),1.0]])],"derivedFrom":subQ0})])],"isStart":false});}
            var Q65;
            {var subQ0=sQuery(id+"F0.wireOp",EDGE,"E37.0");Q65=makeQuery(id+"F2.opExtrude","CAP_EDGE",EDGE,{"disambiguationData":[OSD([subQ0]),TDD([makeQuery(id+"F0.imprint","IMPRINT",EDGE,{"disambiguationData":[TD([[makeQuery(id+"F0.imprint","INTERSECT",VERTEX,{"derivedFrom":[sQuery(id+"F0.wireOp",EDGE,"E25"),subQ0]}),1.0]])],"derivedFrom":subQ0})])],"isStart":false});}
            var Q66;
            {var subQ0=sQuery(id+"F0.wireOp",EDGE,"E37.0");Q66=makeQuery(id+"F2.opExtrude","CAP_EDGE",EDGE,{"disambiguationData":[OSD([subQ0]),TDD([makeQuery(id+"F0.imprint","IMPRINT",EDGE,{"disambiguationData":[TD([[makeQuery(id+"F0.imprint","INTERSECT",VERTEX,{"derivedFrom":[sQuery(id+"F0.wireOp",EDGE,"E22"),subQ0]}),1.0]])],"derivedFrom":subQ0})])],"isStart":false});}
            var Q67;
            {var subQ0=sQuery(id+"F0.wireOp",EDGE,"E38.0");Q67=makeQuery(id+"F2.opExtrude","CAP_EDGE",EDGE,{"disambiguationData":[OSD([subQ0]),TDD([makeQuery(id+"F0.imprint","IMPRINT",EDGE,{"disambiguationData":[TD([[makeQuery(id+"F0.imprint","INTERSECT",VERTEX,{"derivedFrom":[sQuery(id+"F0.wireOp",EDGE,"E22"),subQ0]}),1.0]])],"derivedFrom":subQ0})])],"isStart":false});}
            var Q68;
            {var subQ0=sQuery(id+"F0.wireOp",EDGE,"E35.0");Q68=makeQuery(id+"F2.opExtrude","CAP_EDGE",EDGE,{"disambiguationData":[OSD([subQ0]),TDD([makeQuery(id+"F0.imprint","IMPRINT",EDGE,{"disambiguationData":[TD([[makeQuery(id+"F0.imprint","INTERSECT",VERTEX,{"derivedFrom":[sQuery(id+"F0.wireOp",EDGE,"E22"),subQ0]}),1.0]])],"derivedFrom":subQ0})])],"isStart":false});}
            var Q69;
            {var subQ0=sQuery(id+"F0.wireOp",EDGE,"E36.MirrorCS");Q69=makeQuery(id+"F2.opExtrude","CAP_EDGE",EDGE,{"disambiguationData":[OSD([subQ0]),TDD([makeQuery(id+"F0.imprint","IMPRINT",EDGE,{"disambiguationData":[TD([[makeQuery(id+"F0.imprint","INTERSECT",VERTEX,{"derivedFrom":[sQuery(id+"F0.wireOp",EDGE,"E22"),subQ0]}),1.0]])],"derivedFrom":subQ0})])],"isStart":false});}
            var Q70;
            {var subQ0=sQuery(id+"F0.wireOp",EDGE,"E33.0");Q70=makeQuery(id+"F2.opExtrude","CAP_EDGE",EDGE,{"disambiguationData":[OSD([subQ0]),TDD([makeQuery(id+"F0.imprint","IMPRINT",EDGE,{"disambiguationData":[TD([[makeQuery(id+"F0.imprint","INTERSECT",VERTEX,{"derivedFrom":[sQuery(id+"F0.wireOp",EDGE,"E22"),subQ0]}),1.0]])],"derivedFrom":subQ0})])],"isStart":false});}
            var Q71;
            {var subQ0=sQuery(id+"F0.wireOp",EDGE,"E34.MirrorCS");Q71=makeQuery(id+"F2.opExtrude","CAP_EDGE",EDGE,{"disambiguationData":[OSD([subQ0]),TDD([makeQuery(id+"F0.imprint","IMPRINT",EDGE,{"disambiguationData":[TD([[makeQuery(id+"F0.imprint","INTERSECT",VERTEX,{"derivedFrom":[sQuery(id+"F0.wireOp",EDGE,"E22"),subQ0]}),1.0]])],"derivedFrom":subQ0})])],"isStart":false});}
            var Q72;
            {var subQ0=sQuery(id+"F0.wireOp",EDGE,"E31.0");Q72=makeQuery(id+"F2.opExtrude","CAP_EDGE",EDGE,{"disambiguationData":[OSD([subQ0]),TDD([makeQuery(id+"F0.imprint","IMPRINT",EDGE,{"disambiguationData":[TD([[makeQuery(id+"F0.imprint","INTERSECT",VERTEX,{"derivedFrom":[sQuery(id+"F0.wireOp",EDGE,"E22"),subQ0]}),1.0]])],"derivedFrom":subQ0})])],"isStart":false});}
            var Q73;
            {var subQ0=sQuery(id+"F0.wireOp",EDGE,"E27");Q73=makeQuery(id+"F2.opExtrude","CAP_EDGE",EDGE,{"disambiguationData":[OSD([subQ0]),TDD([makeQuery(id+"F0.imprint","IMPRINT",EDGE,{"disambiguationData":[TD([[makeQuery(id+"F0.imprint","INTERSECT",VERTEX,{"derivedFrom":[subQ0,sQuery(id+"F0.wireOp",EDGE,"E29")]}),-1.0]])],"derivedFrom":subQ0})])],"isStart":false});}
            fillet(context, id + "F5", {"entities" : qUnion([Q0, Q1, Q2, Q3, Q4, Q5, Q6, Q7, Q8, Q9, Q10, Q11, Q12, Q13, Q14, Q15, Q16, Q17, Q18, Q19, Q20, Q21, Q22, Q23, Q24, Q25, Q26, Q27, Q28, Q29, Q30, Q31, Q32, Q33, Q34, Q35, Q36, Q37, Q38, Q39, Q40, Q41, Q42, Q43, Q44, Q45, Q46, Q47, Q48, Q49, Q50, Q51, Q52, Q53, Q54, Q55, Q56, Q57, Q58, Q59, Q60, Q61, Q62, Q63, Q64, Q65, Q66, Q67, Q68, Q69, Q70, Q71, Q72, Q73]), "radius" : 0.5 * mm, "tangentPropagation" : true, "allowEdgeOverflow" : false});
        }
        {
            var Q0;
            Q0=makeQuery(id+"F1.opExtrude","SWEPT_FACE",FACE,{"disambiguationData":[OSD([sQuery(id+"F0.wireOp",EDGE,"E4")])]});
            var sketch = newSketch(context, id + "F6", { "sketchPlane" : qUnion([Q0])});
            skLineSegment(sketch, "E45.0", {"start": v(-19.33, 1.5) * mm, "end": v(-19.33, 0) * mm});
            skArc(sketch, "E45.1", {"start": v(-20.33, 1.5) * mm, "mid": v(-19.83, 2) * mm, "end": v(-19.33, 1.5) * mm});
            skLineSegment(sketch, "E45.2", {"start": v(-20.33, 1.5) * mm, "end": v(-20.33, 0) * mm});
            skLineSegment(sketch, "E46", {"start": v(-20.33, 0) * mm, "end": v(-19.33, 0) * mm});
            skLineSegment(sketch, "E47.0", {"start": v(-40.67, 1.5) * mm, "end": v(-40.67, 0) * mm});
            skArc(sketch, "E47.1", {"start": v(-40.67, 1.5) * mm, "mid": v(-40.17, 2) * mm, "end": v(-39.67, 1.5) * mm});
            skLineSegment(sketch, "E47.2", {"start": v(-39.67, 1.5) * mm, "end": v(-39.67, 0) * mm});
            skLineSegment(sketch, "E48", {"start": v(-40.67, 0) * mm, "end": v(-39.67, 0) * mm});
            skSolve(sketch);
        }
        {
            var Q0;
            Q0=qSketchRegion(id+"F6",true);
            var Q1;
            Q1=makeQuery(id+"F1.opExtrude","SWEPT_FACE",FACE,{"disambiguationData":[OSD([sQuery(id+"F0.wireOp",EDGE,"E8")])]});
            var Q2;
            Q2=makeQuery(id+"F1.opExtrude","SWEPT_FACE",FACE,{"disambiguationData":[OSD([sQuery(id+"F0.wireOp",EDGE,"E6")])]});
            extrude(context, id + "F7", {"entities" : qUnion([Q0]), "operationType" : NewBodyOperationType.ADD, "endBound" : BoundingType.UP_TO_SURFACE, "endBoundEntityFace" : qUnion([Q1]), "depth" : 25 * mm});
        }
        {
            var Q0;
            Q0=makeQuery(id+"F1.opExtrude","SWEPT_FACE",FACE,{"disambiguationData":[OSD([sQuery(id+"F0.wireOp",EDGE,"E6")])]});
            var sketch = newSketch(context, id + "F8", { "sketchPlane" : qUnion([Q0])});
            skLineSegment(sketch, "E49.0", {"start": v(40.67, 1.5) * mm, "end": v(40.67, 0) * mm});
            skArc(sketch, "E49.1", {"start": v(39.67, 1.5) * mm, "mid": v(40.17, 2) * mm, "end": v(40.67, 1.5) * mm});
            skLineSegment(sketch, "E49.2", {"start": v(39.67, 1.5) * mm, "end": v(39.67, 0) * mm});
            skLineSegment(sketch, "E50.0", {"start": v(19.33, 1.5) * mm, "end": v(19.33, 0) * mm});
            skArc(sketch, "E50.1", {"start": v(19.33, 1.5) * mm, "mid": v(19.83, 2) * mm, "end": v(20.33, 1.5) * mm});
            skLineSegment(sketch, "E50.2", {"start": v(20.33, 1.5) * mm, "end": v(20.33, 0) * mm});
            skLineSegment(sketch, "E51", {"start": v(19.33, 0) * mm, "end": v(20.33, 0) * mm});
            skLineSegment(sketch, "E52", {"start": v(39.67, 0) * mm, "end": v(40.67, 0) * mm});
            skSolve(sketch);
        }
        {
            var Q0;
            Q0=qSketchRegion(id+"F8",true);
            extrude(context, id + "F9", {"entities" : qUnion([Q0]), "operationType" : NewBodyOperationType.ADD, "endBound" : BoundingType.UP_TO_NEXT, "depth" : 25 * mm});
        }
        {
            var Q0;
            Q0=qCreatedBy(makeId("Top.planeOp"),FACE);
            var sketch = newSketch(context, id + "F10", { "sketchPlane" : qUnion([Q0])});
            skPoint(sketch, "E53.0", {"position": v(62, 63) * mm});
            skLineSegment(sketch, "E54", {"start": v(62, 63) * mm, "end": v(67.5, 63) * mm});
            skLineSegment(sketch, "E55", {"start": v(67.5, 63) * mm, "end": v(67.5, -3) * mm});
            skPoint(sketch, "E56.0", {"position": v(59, 60) * mm});
            skLineSegment(sketch, "E57.0", {"start": v(62, -3) * mm, "end": v(62, 63) * mm});
            skLineSegment(sketch, "E58", {"start": v(62, 60) * mm, "end": v(67.5, 60) * mm});
            skLineSegment(sketch, "E59", {"start": v(67.5, -3) * mm, "end": v(62, -3) * mm});
            skPoint(sketch, "E60.0", {"position": v(59, 0) * mm});
            skLineSegment(sketch, "E61", {"start": v(62, 0) * mm, "end": v(67.5, 0) * mm});
            skSolve(sketch);
        }
        {
            var Q0;
            {var subQ0=sQuery(id+"F10.wireOp",EDGE,"E54");Q0=makeQuery(id+"F10.imprint","IMPRINT",FACE,{"disambiguationData":[TD([[makeQuery(id+"F10.imprint","IMPRINT",EDGE,{"derivedFrom":subQ0}),-1.0]])]});}
            var Q1;
            {var subQ0=sQuery(id+"F10.wireOp",EDGE,"E59");Q1=makeQuery(id+"F10.imprint","IMPRINT",FACE,{"disambiguationData":[TD([[makeQuery(id+"F10.imprint","IMPRINT",EDGE,{"derivedFrom":subQ0}),-1.0]])]});}
            var Q2;
            Q2=makeQuery(id+"F1.opExtrude","CAP_FACE",FACE,{"disambiguationData":[OSD([sQuery(id+"F0.wireOp",EDGE,"E0.left"),sQuery(id+"F0.wireOp",EDGE,"E0.right"),sQuery(id+"F0.wireOp",EDGE,"E4"),sQuery(id+"F0.wireOp",EDGE,"E6"),sQuery(id+"F0.wireOp",EDGE,"E7"),sQuery(id+"F0.wireOp",EDGE,"E8"),sQuery(id+"F0.wireOp",EDGE,"E11"),sQuery(id+"F0.wireOp",EDGE,"E12"),sQuery(id+"F0.wireOp",EDGE,"E13.left"),sQuery(id+"F0.wireOp",EDGE,"E15.left"),sQuery(id+"F0.wireOp",EDGE,"E18.5.0.3"),sQuery(id+"F0.wireOp",EDGE,"E18.5.1.3"),sQuery(id+"F0.wireOp",EDGE,"E18.5.2.3"),sQuery(id+"F0.wireOp",EDGE,"E18.5.3.3"),sQuery(id+"F0.wireOp",EDGE,"E18.5.4.3"),sQuery(id+"F0.wireOp",EDGE,"E18.5.5.3"),sQuery(id+"F0.wireOp",EDGE,"E0.bottom"),sQuery(id+"F0.wireOp",EDGE,"E19.top"),sQuery(id+"F0.wireOp",EDGE,"E19.left"),sQuery(id+"F0.wireOp",EDGE,"E19.right"),sQuery(id+"F0.wireOp",EDGE,"E0.top"),sQuery(id+"F0.wireOp",EDGE,"E20.top"),sQuery(id+"F0.wireOp",EDGE,"E20.left"),sQuery(id+"F0.wireOp",EDGE,"E20.right"),sQuery(id+"F0.wireOp",EDGE,"E22"),sQuery(id+"F0.wireOp",EDGE,"E23"),sQuery(id+"F0.wireOp",EDGE,"E29"),sQuery(id+"F0.wireOp",EDGE,"E30.8.0")])],"isStart":false});
            extrude(context, id + "F11", {"entities" : qUnion([Q0, Q1]), "operationType" : NewBodyOperationType.ADD, "endBound" : BoundingType.UP_TO_SURFACE, "endBoundEntityFace" : qUnion([Q2]), "depth" : 25 * mm});
        }
        {
            var Q0;
            {var subQ0=sQuery(id+"F10.wireOp",EDGE,"E55");Q0=makeQuery(id+"F11.opExtrude","SWEPT_FACE",FACE,{"disambiguationData":[OSD([subQ0]),TDD([makeQuery(id+"F10.imprint","IMPRINT",EDGE,{"disambiguationData":[TD([[makeQuery(id+"F10.imprint","INTERSECT",VERTEX,{"derivedFrom":[sQuery(id+"F10.wireOp",EDGE,"E54"),subQ0]}),-1.0]])],"derivedFrom":subQ0})])]});}
            cPlane(context, id + "F12", {"entities" : qUnion([Q0]), "cplaneType" : CPlaneType.OFFSET, "offset" : 0 * mm, "width" : 150 * mm, "height" : 150 * mm});
        }
        {
            var Q0;
            Q0=makeQuery(id+"F1.opExtrude","SWEPT_BODY",BODY,{"disambiguationData":[OSD([sQuery(id+"F0.wireOp",EDGE,"E0.left"),sQuery(id+"F0.wireOp",EDGE,"E0.right"),sQuery(id+"F0.wireOp",EDGE,"E4"),sQuery(id+"F0.wireOp",EDGE,"E6"),sQuery(id+"F0.wireOp",EDGE,"E7"),sQuery(id+"F0.wireOp",EDGE,"E8"),sQuery(id+"F0.wireOp",EDGE,"E11"),sQuery(id+"F0.wireOp",EDGE,"E12"),sQuery(id+"F0.wireOp",EDGE,"E13.left"),sQuery(id+"F0.wireOp",EDGE,"E15.left"),sQuery(id+"F0.wireOp",EDGE,"E18.5.0.3"),sQuery(id+"F0.wireOp",EDGE,"E18.5.1.3"),sQuery(id+"F0.wireOp",EDGE,"E18.5.2.3"),sQuery(id+"F0.wireOp",EDGE,"E18.5.3.3"),sQuery(id+"F0.wireOp",EDGE,"E18.5.4.3"),sQuery(id+"F0.wireOp",EDGE,"E18.5.5.3"),sQuery(id+"F0.wireOp",EDGE,"E0.bottom"),sQuery(id+"F0.wireOp",EDGE,"E19.top"),sQuery(id+"F0.wireOp",EDGE,"E19.left"),sQuery(id+"F0.wireOp",EDGE,"E19.right"),sQuery(id+"F0.wireOp",EDGE,"E0.top"),sQuery(id+"F0.wireOp",EDGE,"E20.top"),sQuery(id+"F0.wireOp",EDGE,"E20.left"),sQuery(id+"F0.wireOp",EDGE,"E20.right"),sQuery(id+"F0.wireOp",EDGE,"E22"),sQuery(id+"F0.wireOp",EDGE,"E23"),sQuery(id+"F0.wireOp",EDGE,"E29"),sQuery(id+"F0.wireOp",EDGE,"E30.8.0")])]});
            var Q1;
            Q1=qCreatedBy(id+"F12.planeOp",FACE);
            mirror(context, id + "F13", {"operationType" : NewBodyOperationType.ADD, "entities" : qUnion([Q0]), "mirrorPlane" : qUnion([Q1])});
        }
    });
